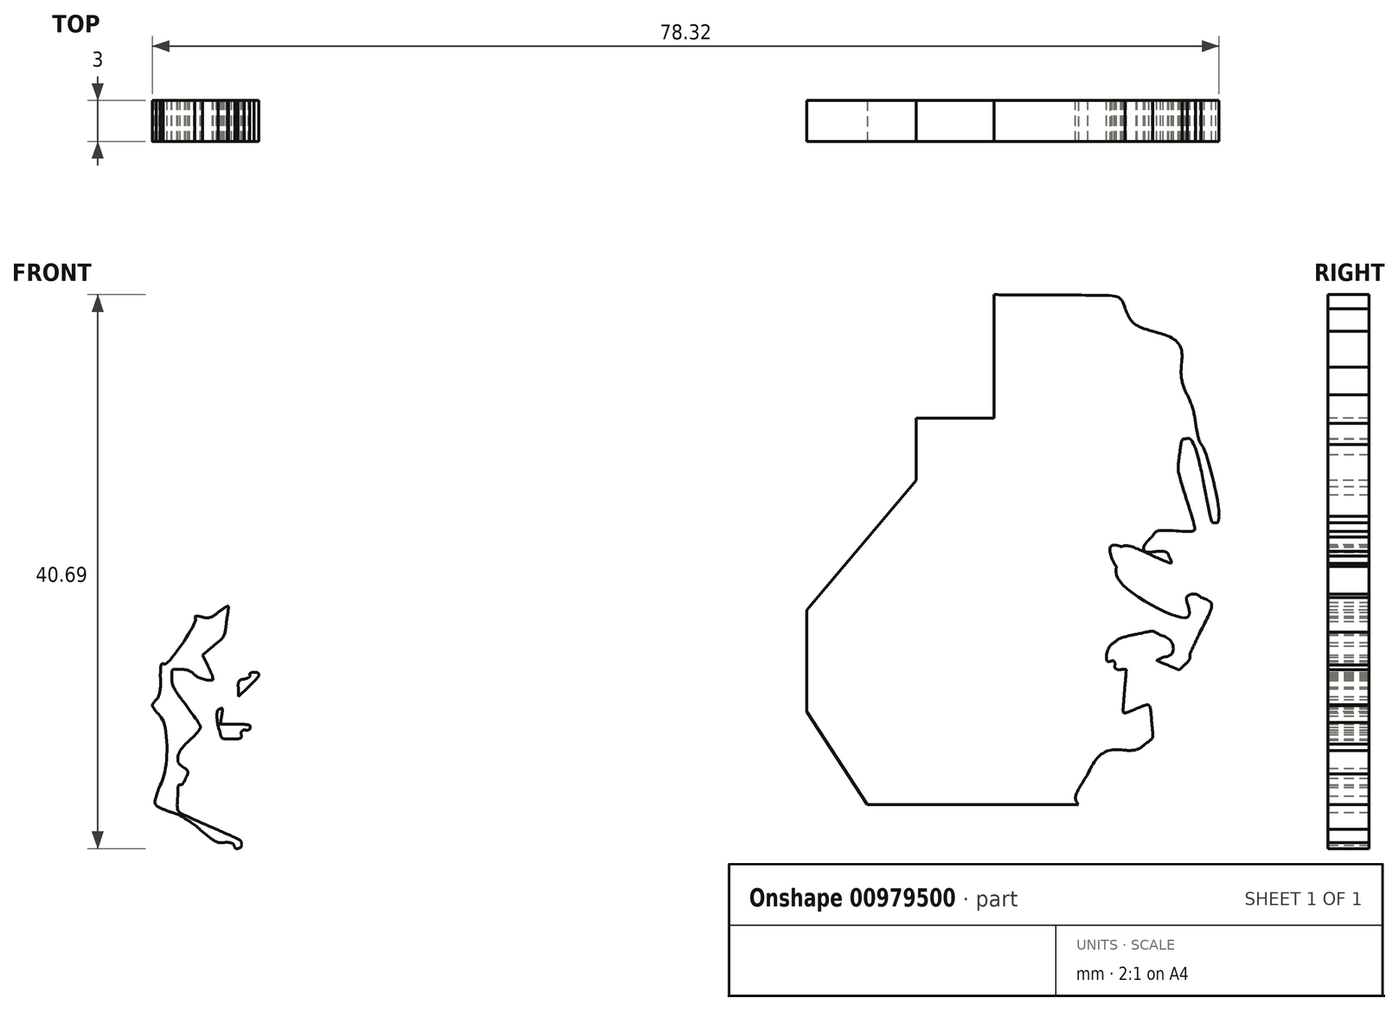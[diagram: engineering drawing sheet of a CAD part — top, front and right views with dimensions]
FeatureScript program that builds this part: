
annotation { "Feature Type Name" : "Feature", "Feature Type Description" : "" }
export const myFeature = defineFeature(function(context is Context, id is Id, definition is map)
    precondition{}
    {
        {
            var Q0;
            Q0=qCreatedBy(makeId("Front.planeOp"),FACE);
            var sketch = newSketch(context, id + "F0", { "sketchPlane" : qUnion([Q0])});
            skLineSegment(sketch, "E0", {"start": v(-32.88, 19.2) * mm, "end": v(-32.1, 20.83) * mm});
            skLineSegment(sketch, "E1", {"start": v(-32.1, 20.83) * mm, "end": v(-32.57, 22.16) * mm});
            skLineSegment(sketch, "E2", {"start": v(-27.5, 16.63) * mm, "end": v(-26.83, 16.28) * mm});
            skLineSegment(sketch, "E3", {"start": v(-26.83, 16.28) * mm, "end": v(-26.97, 16.83) * mm});
            skLineSegment(sketch, "E4", {"start": v(-24.85, 15.67) * mm, "end": v(-25.4, 15.88) * mm});
            skLineSegment(sketch, "E5", {"start": v(-25.4, 15.88) * mm, "end": v(-25.34, 18.4) * mm});
            skLineSegment(sketch, "E6", {"start": v(-1.75, 78.04) * mm, "end": v(-0.2, 79.6) * mm});
            skLineSegment(sketch, "E7", {"start": v(-0.2, 79.6) * mm, "end": v(1.27, 79.6) * mm});
            skLineSegment(sketch, "E8", {"start": v(38.3, 44.26) * mm, "end": v(38.3, 43.17) * mm});
            skLineSegment(sketch, "E9", {"start": v(38.3, 43.17) * mm, "end": v(37.62, 43.24) * mm});
            skLineSegment(sketch, "E10", {"start": v(39.65, -31.25) * mm, "end": v(39.52, -33.83) * mm});
            skLineSegment(sketch, "E11", {"start": v(39.52, -33.83) * mm, "end": v(40.18, -34.42) * mm});
            skLineSegment(sketch, "E12", {"start": v(1.4, 79.08) * mm, "end": v(0.3, 79.22) * mm});
            skLineSegment(sketch, "E13", {"start": v(0.3, 79.22) * mm, "end": v(-1.23, 77.67) * mm});
            skLineSegment(sketch, "E14", {"start": v(-12.51, 69.45) * mm, "end": v(-13.4, 69.45) * mm});
            skLineSegment(sketch, "E15", {"start": v(-13.4, 69.45) * mm, "end": v(-13.27, 67.07) * mm});
            skLineSegment(sketch, "E16", {"start": v(-18.31, 54.9) * mm, "end": v(-18.88, 53.48) * mm});
            skLineSegment(sketch, "E17", {"start": v(-18.88, 53.48) * mm, "end": v(-18.43, 53.1) * mm});
            skLineSegment(sketch, "E18", {"start": v(-20.94, 40.45) * mm, "end": v(-21.55, 40.45) * mm});
            skLineSegment(sketch, "E19", {"start": v(-21.55, 40.45) * mm, "end": v(-21.44, 41.8) * mm});
            skLineSegment(sketch, "E20", {"start": v(-24.47, 43.3) * mm, "end": v(-25.23, 42.61) * mm});
            skLineSegment(sketch, "E21", {"start": v(-25.23, 42.61) * mm, "end": v(-24.8, 41.05) * mm});
            skLineSegment(sketch, "E22", {"start": v(-37.96, -16.18) * mm, "end": v(-37.29, -17.23) * mm});
            skLineSegment(sketch, "E23", {"start": v(-37.29, -17.23) * mm, "end": v(-37.41, -20.41) * mm});
            skLineSegment(sketch, "E24", {"start": v(-30.4, -60.92) * mm, "end": v(-31.42, -62.04) * mm});
            skLineSegment(sketch, "E25", {"start": v(-31.42, -62.04) * mm, "end": v(-30.9, -63.02) * mm});
            skLineSegment(sketch, "E26", {"start": v(-36.35, 33.14) * mm, "end": v(-36.7, 33.88) * mm});
            skLineSegment(sketch, "E27", {"start": v(-36.7, 33.88) * mm, "end": v(-35.92, 34.57) * mm});
            skLineSegment(sketch, "E28", {"start": v(-34.09, 31.43) * mm, "end": v(-34.09, 30.84) * mm});
            skLineSegment(sketch, "E29", {"start": v(-34.09, 30.84) * mm, "end": v(-33.35, 31.56) * mm});
            skFitSpline(sketch, "E30", {"points": [v(-13.45, -80.7) * mm, v(-14.26, -80.4) * mm, v(-15.79, -79.86) * mm, v(-16.84, -79.51) * mm]});
            skFitSpline(sketch, "E31", {"points": [v(-16.84, -79.51) * mm, v(-20.43, -78.33) * mm, v(-20.6, -78.25) * mm, v(-21.55, -77.26) * mm]});
            skFitSpline(sketch, "E32", {"points": [v(-21.55, -77.26) * mm, v(-22.07, -76.72) * mm, v(-23.66, -74.52) * mm, v(-25.09, -72.37) * mm]});
            skFitSpline(sketch, "E33", {"points": [v(-25.09, -72.37) * mm, v(-26.52, -70.21) * mm, v(-28.36, -67.6) * mm, v(-29.19, -66.55) * mm]});
            skFitSpline(sketch, "E34", {"points": [v(-29.19, -66.55) * mm, v(-30.6, -64.76) * mm, v(-31.97, -62.53) * mm, v(-31.97, -62.03) * mm]});
            skFitSpline(sketch, "E35", {"points": [v(-31.97, -62.03) * mm, v(-31.97, -61.91) * mm, v(-31.5, -61.27) * mm, v(-30.92, -60.6) * mm]});
            skFitSpline(sketch, "E36", {"points": [v(-30.92, -60.6) * mm, v(-29.85, -59.39) * mm, v(-29, -57.92) * mm, v(-29, -57.28) * mm]});
            skFitSpline(sketch, "E37", {"points": [v(-29, -57.28) * mm, v(-29, -57.08) * mm, v(-29.34, -56.3) * mm, v(-29.75, -55.53) * mm]});
            skFitSpline(sketch, "E38", {"points": [v(-29.75, -55.53) * mm, v(-30.57, -53.98) * mm, v(-30.63, -53.57) * mm, v(-30.2, -52.72) * mm]});
            skFitSpline(sketch, "E39", {"points": [v(-30.2, -52.72) * mm, v(-29.95, -52.26) * mm, v(-29.92, -51.55) * mm, v(-30.04, -49.29) * mm]});
            skFitSpline(sketch, "E40", {"points": [v(-30.04, -49.29) * mm, v(-30.2, -46.13) * mm, v(-30.12, -46.32) * mm, v(-32.34, -43.6) * mm]});
            skFitSpline(sketch, "E41", {"points": [v(-32.34, -43.6) * mm, v(-32.83, -43) * mm, v(-33.38, -42.01) * mm, v(-33.55, -41.42) * mm]});
            skFitSpline(sketch, "E42", {"points": [v(-33.55, -41.42) * mm, v(-33.73, -40.84) * mm, v(-34.2, -39.94) * mm, v(-34.62, -39.44) * mm]});
            skFitSpline(sketch, "E43", {"points": [v(-34.62, -39.44) * mm, v(-36.03, -37.71) * mm, v(-36.52, -35.97) * mm, v(-35.98, -34.56) * mm]});
            skFitSpline(sketch, "E44", {"points": [v(-35.98, -34.56) * mm, v(-35.86, -34.24) * mm, v(-35.38, -33.57) * mm, v(-34.92, -33.07) * mm]});
            skFitSpline(sketch, "E45", {"points": [v(-34.92, -33.07) * mm, v(-33.97, -32.03) * mm, v(-34, -32.17) * mm, v(-34.37, -30.78) * mm]});
            skFitSpline(sketch, "E46", {"points": [v(-34.37, -30.78) * mm, v(-34.75, -29.38) * mm, v(-35.2, -28.53) * mm, v(-36.46, -26.88) * mm]});
            skFitSpline(sketch, "E47", {"points": [v(-36.46, -26.88) * mm, v(-37.04, -26.13) * mm, v(-37.61, -25.27) * mm, v(-37.73, -24.97) * mm]});
            skFitSpline(sketch, "E48", {"points": [v(-37.73, -24.97) * mm, v(-37.97, -24.39) * mm, v(-38.06, -21.07) * mm, v(-37.9, -18.8) * mm]});
            skFitSpline(sketch, "E49", {"points": [v(-37.9, -18.8) * mm, v(-37.82, -17.55) * mm, v(-37.87, -17.35) * mm, v(-38.39, -16.67) * mm]});
            skFitSpline(sketch, "E50", {"points": [v(-38.39, -16.67) * mm, v(-39.51, -15.19) * mm, v(-39.6, -12.77) * mm, v(-38.72, -7.81) * mm]});
            skFitSpline(sketch, "E51", {"points": [v(-38.72, -7.81) * mm, v(-38.24, -5.14) * mm, v(-38.31, -2.1) * mm, v(-38.87, -1) * mm]});
            skFitSpline(sketch, "E52", {"points": [v(-38.87, -1) * mm, v(-39.1, -0.56) * mm, v(-39.11, -0.29) * mm, v(-38.94, 0.17) * mm]});
            skFitSpline(sketch, "E53", {"points": [v(-38.94, 0.17) * mm, v(-38.62, 1) * mm, v(-38.87, 3.38) * mm, v(-39.5, 5.38) * mm]});
            skFitSpline(sketch, "E54", {"points": [v(-39.5, 5.38) * mm, v(-39.78, 6.29) * mm, v(-40.01, 7.26) * mm, v(-40.01, 7.54) * mm]});
            skFitSpline(sketch, "E55", {"points": [v(-40.01, 7.54) * mm, v(-40.01, 7.83) * mm, v(-39.68, 9.05) * mm, v(-39.27, 10.27) * mm]});
            skFitSpline(sketch, "E56", {"points": [v(-39.27, 10.27) * mm, v(-38.41, 12.85) * mm, v(-38.39, 13.06) * mm, v(-38.96, 13.2) * mm]});
            skFitSpline(sketch, "E57", {"points": [v(-38.96, 13.2) * mm, v(-39.71, 13.4) * mm, v(-39.48, 14.32) * mm, v(-38.38, 15.5) * mm]});
            skFitSpline(sketch, "E58", {"points": [v(-38.38, 15.5) * mm, v(-36.83, 17.16) * mm, v(-35.68, 17.57) * mm, v(-34.74, 16.8) * mm]});
            skFitSpline(sketch, "E59", {"points": [v(-34.74, 16.8) * mm, v(-34.08, 16.26) * mm, v(-32.77, 13.22) * mm, v(-32.66, 11.98) * mm]});
            skFitSpline(sketch, "E60", {"points": [v(-32.66, 11.98) * mm, v(-32.55, 10.86) * mm, v(-32.37, 10.61) * mm, v(-31.6, 10.6) * mm]});
            skFitSpline(sketch, "E61", {"points": [v(-31.6, 10.6) * mm, v(-31, 10.6) * mm, v(-30.96, 11.24) * mm, v(-31.55, 11.77) * mm]});
            skFitSpline(sketch, "E62", {"points": [v(-31.55, 11.77) * mm, v(-31.84, 12.03) * mm, v(-31.97, 12.42) * mm, v(-31.97, 13) * mm]});
            skFitSpline(sketch, "E63", {"points": [v(-31.97, 13) * mm, v(-31.97, 14.32) * mm, v(-32.62, 16.12) * mm, v(-33.18, 16.38) * mm]});
            skFitSpline(sketch, "E64", {"points": [v(-33.18, 16.38) * mm, v(-33.86, 16.69) * mm, v(-33.8, 17.27) * mm, v(-32.88, 19.2) * mm]});
            skFitSpline(sketch, "E65", {"points": [v(-32.57, 22.16) * mm, v(-32.82, 22.9) * mm, v(-33.03, 23.65) * mm, v(-33.03, 23.83) * mm]});
            skFitSpline(sketch, "E66", {"points": [v(-33.03, 23.83) * mm, v(-33.03, 24.1) * mm, v(-33.14, 24.14) * mm, v(-33.5, 24.01) * mm]});
            skFitSpline(sketch, "E67", {"points": [v(-33.5, 24.01) * mm, v(-33.77, 23.92) * mm, v(-34.4, 23.84) * mm, v(-34.93, 23.84) * mm]});
            skFitSpline(sketch, "E68", {"points": [v(-34.93, 23.84) * mm, v(-35.84, 23.83) * mm, v(-35.89, 23.86) * mm, v(-35.95, 24.48) * mm]});
            skFitSpline(sketch, "E69", {"points": [v(-35.95, 24.48) * mm, v(-36.05, 25.55) * mm, v(-34.78, 26.27) * mm, v(-32.78, 26.27) * mm]});
            skFitSpline(sketch, "E70", {"points": [v(-32.78, 26.27) * mm, v(-31.93, 26.27) * mm, v(-31.64, 26.16) * mm, v(-31.1, 25.65) * mm]});
            skFitSpline(sketch, "E71", {"points": [v(-31.1, 25.65) * mm, v(-30.75, 25.3) * mm, v(-30.32, 25.08) * mm, v(-30.15, 25.14) * mm]});
            skFitSpline(sketch, "E72", {"points": [v(-30.15, 25.14) * mm, v(-29.7, 25.31) * mm, v(-29.77, 25.47) * mm, v(-30.7, 26.37) * mm]});
            skFitSpline(sketch, "E73", {"points": [v(-30.7, 26.37) * mm, v(-31.5, 27.15) * mm, v(-31.55, 27.27) * mm, v(-31.55, 28.43) * mm]});
            skFitSpline(sketch, "E74", {"points": [v(-31.55, 28.43) * mm, v(-31.55, 29.6) * mm, v(-31.52, 29.65) * mm, v(-31.02, 29.65) * mm]});
            skFitSpline(sketch, "E75", {"points": [v(-31.02, 29.65) * mm, v(-30.7, 29.65) * mm, v(-30.49, 29.53) * mm, v(-30.49, 29.36) * mm]});
            skFitSpline(sketch, "E76", {"points": [v(-30.49, 29.36) * mm, v(-30.49, 28.94) * mm, v(-28.82, 27.75) * mm, v(-28.24, 27.75) * mm]});
            skFitSpline(sketch, "E77", {"points": [v(-28.24, 27.75) * mm, v(-27.83, 27.75) * mm, v(-27.75, 27.6) * mm, v(-27.62, 26.6) * mm]});
            skFitSpline(sketch, "E78", {"points": [v(-27.62, 26.6) * mm, v(-27.46, 25.26) * mm, v(-27.66, 24.55) * mm, v(-28.57, 23.22) * mm]});
            skFitSpline(sketch, "E79", {"points": [v(-28.57, 23.22) * mm, v(-29.21, 22.29) * mm, v(-29.4, 21.61) * mm, v(-29.02, 21.61) * mm]});
            skFitSpline(sketch, "E80", {"points": [v(-29.02, 21.61) * mm, v(-28.66, 21.61) * mm, v(-28.35, 20.18) * mm, v(-28.49, 19.14) * mm]});
            skFitSpline(sketch, "E81", {"points": [v(-28.49, 19.14) * mm, v(-28.66, 17.84) * mm, v(-28.36, 17.07) * mm, v(-27.5, 16.63) * mm]});
            skFitSpline(sketch, "E82", {"points": [v(-26.97, 16.83) * mm, v(-27.1, 17.33) * mm, v(-27.05, 17.38) * mm, v(-26.5, 17.38) * mm]});
            skFitSpline(sketch, "E83", {"points": [v(-26.5, 17.38) * mm, v(-25.81, 17.38) * mm, v(-25.62, 17.08) * mm, v(-25.62, 16.04) * mm]});
            skFitSpline(sketch, "E84", {"points": [v(-25.62, 16.04) * mm, v(-25.62, 15.5) * mm, v(-25.82, 15.19) * mm, v(-26.56, 14.52) * mm]});
            skFitSpline(sketch, "E85", {"points": [v(-26.56, 14.52) * mm, v(-27.09, 14.05) * mm, v(-27.58, 13.4) * mm, v(-27.66, 13.06) * mm]});
            skFitSpline(sketch, "E86", {"points": [v(-27.66, 13.06) * mm, v(-27.79, 12.49) * mm, v(-27.76, 12.45) * mm, v(-27.3, 12.58) * mm]});
            skFitSpline(sketch, "E87", {"points": [v(-27.3, 12.58) * mm, v(-27.01, 12.65) * mm, v(-26.47, 12.72) * mm, v(-26.09, 12.72) * mm]});
            skFitSpline(sketch, "E88", {"points": [v(-26.09, 12.72) * mm, v(-25.47, 12.72) * mm, v(-25.42, 12.76) * mm, v(-25.61, 13.13) * mm]});
            skFitSpline(sketch, "E89", {"points": [v(-25.61, 13.13) * mm, v(-26.02, 13.88) * mm, v(-25.88, 14.6) * mm, v(-25.31, 14.75) * mm]});
            skFitSpline(sketch, "E90", {"points": [v(-25.31, 14.75) * mm, v(-25.03, 14.82) * mm, v(-24.68, 15.01) * mm, v(-24.55, 15.17) * mm]});
            skFitSpline(sketch, "E91", {"points": [v(-24.55, 15.17) * mm, v(-24.35, 15.4) * mm, v(-24.42, 15.5) * mm, v(-24.85, 15.67) * mm]});
            skFitSpline(sketch, "E92", {"points": [v(-25.34, 18.4) * mm, v(-25.28, 20.49) * mm, v(-25.2, 21.05) * mm, v(-24.84, 21.66) * mm]});
            skFitSpline(sketch, "E93", {"points": [v(-24.84, 21.66) * mm, v(-24.6, 22.07) * mm, v(-24.33, 22.91) * mm, v(-24.25, 23.54) * mm]});
            skFitSpline(sketch, "E94", {"points": [v(-24.25, 23.54) * mm, v(-24.05, 24.98) * mm, v(-23.67, 25.42) * mm, v(-22.64, 25.42) * mm]});
            skFitSpline(sketch, "E95", {"points": [v(-22.64, 25.42) * mm, v(-21.97, 25.42) * mm, v(-21.73, 25.28) * mm, v(-21.09, 24.54) * mm]});
            skFitSpline(sketch, "E96", {"points": [v(-21.09, 24.54) * mm, v(-20.67, 24.05) * mm, v(-20.32, 23.55) * mm, v(-20.32, 23.43) * mm]});
            skFitSpline(sketch, "E97", {"points": [v(-20.32, 23.43) * mm, v(-20.3, 22.93) * mm, v(-19.5, 25.15) * mm, v(-19.5, 25.74) * mm]});
            skFitSpline(sketch, "E98", {"points": [v(-19.5, 25.74) * mm, v(-19.48, 26.68) * mm, v(-19.75, 27) * mm, v(-20.27, 26.68) * mm]});
            skFitSpline(sketch, "E99", {"points": [v(-20.27, 26.68) * mm, v(-20.84, 26.32) * mm, v(-23.7, 26.75) * mm, v(-24.99, 27.38) * mm]});
            skFitSpline(sketch, "E100", {"points": [v(-24.99, 27.38) * mm, v(-26.7, 28.23) * mm, v(-27.27, 29.95) * mm, v(-26.55, 32.07) * mm]});
            skFitSpline(sketch, "E101", {"points": [v(-26.55, 32.07) * mm, v(-26.23, 33) * mm, v(-26.23, 33.13) * mm, v(-26.58, 33.9) * mm]});
            skFitSpline(sketch, "E102", {"points": [v(-26.58, 33.9) * mm, v(-27.04, 34.91) * mm, v(-26.9, 36) * mm, v(-26.2, 36.92) * mm]});
            skFitSpline(sketch, "E103", {"points": [v(-26.2, 36.92) * mm, v(-24.96, 38.54) * mm, v(-24.76, 39.42) * mm, v(-25.3, 40.73) * mm]});
            skFitSpline(sketch, "E104", {"points": [v(-25.3, 40.73) * mm, v(-25.48, 41.15) * mm, v(-25.62, 41.87) * mm, v(-25.62, 42.33) * mm]});
            skFitSpline(sketch, "E105", {"points": [v(-25.62, 42.33) * mm, v(-25.62, 43.02) * mm, v(-25.5, 43.25) * mm, v(-24.99, 43.62) * mm]});
            skFitSpline(sketch, "E106", {"points": [v(-24.99, 43.62) * mm, v(-24.64, 43.87) * mm, v(-24.35, 44.26) * mm, v(-24.35, 44.48) * mm]});
            skFitSpline(sketch, "E107", {"points": [v(-24.35, 44.48) * mm, v(-24.35, 45.6) * mm, v(-22.43, 46.16) * mm, v(-21.62, 45.29) * mm]});
            skFitSpline(sketch, "E108", {"points": [v(-21.62, 45.29) * mm, v(-21.1, 44.74) * mm, v(-20.66, 42.78) * mm, v(-20.82, 41.8) * mm]});
            skFitSpline(sketch, "E109", {"points": [v(-20.82, 41.8) * mm, v(-20.95, 40.98) * mm, v(-20.5, 40.8) * mm, v(-20.12, 41.5) * mm]});
            skFitSpline(sketch, "E110", {"points": [v(-20.12, 41.5) * mm, v(-20, 41.74) * mm, v(-19.7, 41.93) * mm, v(-19.48, 41.93) * mm]});
            skFitSpline(sketch, "E111", {"points": [v(-19.48, 41.93) * mm, v(-19.2, 41.93) * mm, v(-19.03, 42.12) * mm, v(-18.95, 42.51) * mm]});
            skFitSpline(sketch, "E112", {"points": [v(-18.95, 42.51) * mm, v(-18.9, 42.83) * mm, v(-18.75, 43.5) * mm, v(-18.63, 44) * mm]});
            skFitSpline(sketch, "E113", {"points": [v(-18.63, 44) * mm, v(-18.15, 46.1) * mm, v(-18.46, 46.83) * mm, v(-19.95, 47.1) * mm]});
            skFitSpline(sketch, "E114", {"points": [v(-19.95, 47.1) * mm, v(-21.37, 47.35) * mm, v(-21.68, 48.31) * mm, v(-21.02, 50.45) * mm]});
            skFitSpline(sketch, "E115", {"points": [v(-21.02, 50.45) * mm, v(-20.67, 51.58) * mm, v(-20.6, 51.66) * mm, v(-20, 51.67) * mm]});
            skFitSpline(sketch, "E116", {"points": [v(-20, 51.67) * mm, v(-19.64, 51.67) * mm, v(-19.17, 51.8) * mm, v(-18.94, 51.97) * mm]});
            skFitSpline(sketch, "E117", {"points": [v(-18.94, 51.97) * mm, v(-18.56, 52.25) * mm, v(-18.55, 52.28) * mm, v(-18.9, 52.67) * mm]});
            skFitSpline(sketch, "E118", {"points": [v(-18.9, 52.67) * mm, v(-19.36, 53.18) * mm, v(-19.37, 53.99) * mm, v(-18.93, 55) * mm]});
            skFitSpline(sketch, "E119", {"points": [v(-18.93, 55) * mm, v(-18.26, 56.57) * mm, v(-18.22, 56.96) * mm, v(-18.55, 58.71) * mm]});
            skFitSpline(sketch, "E120", {"points": [v(-18.55, 58.71) * mm, v(-19.05, 61.35) * mm, v(-18.66, 63.1) * mm, v(-17.57, 63.1) * mm]});
            skFitSpline(sketch, "E121", {"points": [v(-17.57, 63.1) * mm, v(-17.13, 63.1) * mm, v(-16.93, 62.86) * mm, v(-16.62, 61.94) * mm]});
            skFitSpline(sketch, "E122", {"points": [v(-16.62, 61.94) * mm, v(-16.19, 60.62) * mm, v(-15.25, 61.36) * mm, v(-15.25, 63.03) * mm]});
            skFitSpline(sketch, "E123", {"points": [v(-15.25, 63.03) * mm, v(-15.25, 63.72) * mm, v(-15.21, 63.77) * mm, v(-14.72, 63.65) * mm]});
            skFitSpline(sketch, "E124", {"points": [v(-14.72, 63.65) * mm, v(-13.88, 63.44) * mm, v(-13.7, 64.21) * mm, v(-13.86, 67.25) * mm]});
            skFitSpline(sketch, "E125", {"points": [v(-13.86, 67.25) * mm, v(-14.01, 70.15) * mm, v(-14.06, 70.07) * mm, v(-12.21, 70.08) * mm]});
            skFitSpline(sketch, "E126", {"points": [v(-12.21, 70.08) * mm, v(-11.52, 70.08) * mm, v(-11.25, 70.23) * mm, v(-10.4, 71.12) * mm]});
            skFitSpline(sketch, "E127", {"points": [v(-10.4, 71.12) * mm, v(-9.38, 72.18) * mm, v(-9.03, 72.34) * mm, v(-6.52, 72.84) * mm]});
            skFitSpline(sketch, "E128", {"points": [v(-6.52, 72.84) * mm, v(-4.93, 73.15) * mm, v(-4.21, 73.78) * mm, v(-3.7, 75.27) * mm]});
            skFitSpline(sketch, "E129", {"points": [v(-3.7, 75.27) * mm, v(-3.38, 76.2) * mm, v(-2.96, 76.8) * mm, v(-1.75, 78.04) * mm]});
            skFitSpline(sketch, "E130", {"points": [v(1.27, 79.6) * mm, v(2.66, 79.6) * mm, v(2.79, 79.65) * mm, v(3.57, 80.36) * mm]});
            skFitSpline(sketch, "E131", {"points": [v(3.57, 80.36) * mm, v(4.72, 81.4) * mm, v(5.62, 81.51) * mm, v(6.84, 80.8) * mm]});
            skFitSpline(sketch, "E132", {"points": [v(6.84, 80.8) * mm, v(7.4, 80.48) * mm, v(8.11, 80.24) * mm, v(8.56, 80.24) * mm]});
            skFitSpline(sketch, "E133", {"points": [v(8.56, 80.24) * mm, v(9.65, 80.24) * mm, v(10.66, 79.76) * mm, v(12.03, 78.58) * mm]});
            skFitSpline(sketch, "E134", {"points": [v(12.03, 78.58) * mm, v(12.68, 78.02) * mm, v(13.76, 77.21) * mm, v(14.43, 76.8) * mm]});
            skFitSpline(sketch, "E135", {"points": [v(14.43, 76.8) * mm, v(16.07, 75.75) * mm, v(16.3, 75.23) * mm, v(16.26, 72.68) * mm]});
            skFitSpline(sketch, "E136", {"points": [v(16.26, 72.68) * mm, v(16.21, 70.3) * mm, v(16.3, 70.06) * mm, v(17.99, 67.97) * mm]});
            skFitSpline(sketch, "E137", {"points": [v(17.99, 67.97) * mm, v(19.34, 66.28) * mm, v(19.58, 65.73) * mm, v(19.78, 63.84) * mm]});
            skFitSpline(sketch, "E138", {"points": [v(19.78, 63.84) * mm, v(19.97, 61.97) * mm, v(20.1, 61.75) * mm, v(21.2, 61.28) * mm]});
            skFitSpline(sketch, "E139", {"points": [v(21.2, 61.28) * mm, v(21.95, 60.97) * mm, v(22.77, 60.9) * mm, v(25.95, 60.87) * mm]});
            skFitSpline(sketch, "E140", {"points": [v(25.95, 60.87) * mm, v(29.47, 60.83) * mm, v(29.87, 60.8) * mm, v(30.78, 60.35) * mm]});
            skFitSpline(sketch, "E141", {"points": [v(30.78, 60.35) * mm, v(31.33, 60.09) * mm, v(31.82, 59.71) * mm, v(31.88, 59.53) * mm]});
            skFitSpline(sketch, "E142", {"points": [v(31.88, 59.53) * mm, v(32.1, 58.78) * mm, v(32.32, 58.58) * mm, v(33.34, 58.19) * mm]});
            skFitSpline(sketch, "E143", {"points": [v(33.34, 58.19) * mm, v(35, 57.54) * mm, v(35.47, 56.96) * mm, v(35.61, 55.41) * mm]});
            skFitSpline(sketch, "E144", {"points": [v(35.61, 55.41) * mm, v(35.68, 54.7) * mm, v(35.93, 53.67) * mm, v(36.17, 53.15) * mm]});
            skFitSpline(sketch, "E145", {"points": [v(36.17, 53.15) * mm, v(36.4, 52.63) * mm, v(36.6, 51.94) * mm, v(36.6, 51.62) * mm]});
            skFitSpline(sketch, "E146", {"points": [v(36.6, 51.62) * mm, v(36.6, 51.3) * mm, v(36.8, 50.55) * mm, v(37.02, 49.93) * mm]});
            skFitSpline(sketch, "E147", {"points": [v(37.02, 49.93) * mm, v(37.7, 48.08) * mm, v(38.3, 45.42) * mm, v(38.3, 44.26) * mm]});
            skFitSpline(sketch, "E148", {"points": [v(37.62, 43.24) * mm, v(36.87, 43.31) * mm, v(36.86, 43.33) * mm, v(36.05, 46.9) * mm]});
            skFitSpline(sketch, "E149", {"points": [v(36.05, 46.9) * mm, v(35.75, 48.23) * mm, v(35.65, 48.45) * mm, v(35.6, 47.92) * mm]});
            skFitSpline(sketch, "E150", {"points": [v(35.6, 47.92) * mm, v(35.56, 47.55) * mm, v(35.72, 46.61) * mm, v(35.96, 45.84) * mm]});
            skFitSpline(sketch, "E151", {"points": [v(35.96, 45.84) * mm, v(36.2, 45.06) * mm, v(36.4, 44.16) * mm, v(36.4, 43.83) * mm]});
            skFitSpline(sketch, "E152", {"points": [v(36.4, 43.83) * mm, v(36.4, 42.72) * mm, v(36.23, 42.57) * mm, v(35.04, 42.57) * mm]});
            skFitSpline(sketch, "E153", {"points": [v(35.04, 42.57) * mm, v(34.35, 42.57) * mm, v(33.78, 42.44) * mm, v(33.53, 42.23) * mm]});
            skFitSpline(sketch, "E154", {"points": [v(33.53, 42.23) * mm, v(33.14, 41.92) * mm, v(33.15, 41.9) * mm, v(33.78, 42.01) * mm]});
            skFitSpline(sketch, "E155", {"points": [v(33.78, 42.01) * mm, v(34.37, 42.1) * mm, v(34.48, 42.05) * mm, v(34.7, 41.5) * mm]});
            skFitSpline(sketch, "E156", {"points": [v(34.7, 41.5) * mm, v(35.23, 40.23) * mm, v(34.46, 39.89) * mm, v(32.77, 40.66) * mm]});
            skFitSpline(sketch, "E157", {"points": [v(32.77, 40.66) * mm, v(30, 41.91) * mm, v(30.46, 40.26) * mm, v(33.3, 38.77) * mm]});
            skFitSpline(sketch, "E158", {"points": [v(33.3, 38.77) * mm, v(34.7, 38.04) * mm, v(35.03, 37.98) * mm, v(35.2, 38.44) * mm]});
            skFitSpline(sketch, "E159", {"points": [v(35.2, 38.44) * mm, v(35.4, 38.97) * mm, v(36.94, 38.86) * mm, v(37.34, 38.29) * mm]});
            skFitSpline(sketch, "E160", {"points": [v(37.34, 38.29) * mm, v(37.8, 37.64) * mm, v(37.75, 36.5) * mm, v(37.25, 35.69) * mm]});
            skFitSpline(sketch, "E161", {"points": [v(37.25, 35.69) * mm, v(37.01, 35.31) * mm, v(36.68, 34.6) * mm, v(36.5, 34.09) * mm]});
            skFitSpline(sketch, "E162", {"points": [v(36.5, 34.09) * mm, v(36.07, 32.87) * mm, v(35.62, 32.4) * mm, v(34.86, 32.4) * mm]});
            skFitSpline(sketch, "E163", {"points": [v(34.86, 32.4) * mm, v(34.06, 32.4) * mm, v(32.85, 32.98) * mm, v(32.57, 33.5) * mm]});
            skFitSpline(sketch, "E164", {"points": [v(32.57, 33.5) * mm, v(32.35, 33.9) * mm, v(32.37, 33.91) * mm, v(33.4, 34.23) * mm]});
            skFitSpline(sketch, "E165", {"points": [v(33.4, 34.23) * mm, v(33.55, 34.27) * mm, v(33.64, 34.43) * mm, v(33.6, 34.58) * mm]});
            skFitSpline(sketch, "E166", {"points": [v(33.6, 34.58) * mm, v(33.47, 34.97) * mm, v(32.1, 35.02) * mm, v(31.26, 34.66) * mm]});
            skFitSpline(sketch, "E167", {"points": [v(31.26, 34.66) * mm, v(30.63, 34.4) * mm, v(30.54, 34.27) * mm, v(30.63, 33.8) * mm]});
            skFitSpline(sketch, "E168", {"points": [v(30.63, 33.8) * mm, v(30.71, 33.37) * mm, v(30.83, 33.27) * mm, v(31.13, 33.37) * mm]});
            skFitSpline(sketch, "E169", {"points": [v(31.13, 33.37) * mm, v(31.68, 33.54) * mm, v(31.8, 33.13) * mm, v(31.57, 31.7) * mm]});
            skFitSpline(sketch, "E170", {"points": [v(31.57, 31.7) * mm, v(31.47, 31.04) * mm, v(31.4, 30.5) * mm, v(31.43, 30.5) * mm]});
            skFitSpline(sketch, "E171", {"points": [v(31.43, 30.5) * mm, v(31.46, 30.5) * mm, v(31.82, 30.65) * mm, v(32.25, 30.82) * mm]});
            skFitSpline(sketch, "E172", {"points": [v(32.25, 30.82) * mm, v(33.01, 31.14) * mm, v(33.02, 31.14) * mm, v(33.26, 30.56) * mm]});
            skFitSpline(sketch, "E173", {"points": [v(33.26, 30.56) * mm, v(33.39, 30.24) * mm, v(33.5, 29.43) * mm, v(33.52, 28.77) * mm]});
            skFitSpline(sketch, "E174", {"points": [v(33.52, 28.77) * mm, v(33.55, 27.14) * mm, v(33.03, 26.57) * mm, v(31.4, 26.43) * mm]});
            skFitSpline(sketch, "E175", {"points": [v(31.4, 26.43) * mm, v(29.99, 26.32) * mm, v(29.27, 25.83) * mm, v(28.59, 24.5) * mm]});
            skFitSpline(sketch, "E176", {"points": [v(28.59, 24.5) * mm, v(28.09, 23.52) * mm, v(28.09, 23.5) * mm, v(28.46, 22.8) * mm]});
            skFitSpline(sketch, "E177", {"points": [v(28.46, 22.8) * mm, v(29.02, 21.76) * mm, v(28.8, 20.5) * mm, v(27.76, 18.77) * mm]});
            skFitSpline(sketch, "E178", {"points": [v(27.76, 18.77) * mm, v(26.26, 16.28) * mm, v(26.34, 15.6) * mm, v(28.5, 12.89) * mm]});
            skFitSpline(sketch, "E179", {"points": [v(28.5, 12.89) * mm, v(30.07, 10.9) * mm, v(30.64, 9.85) * mm, v(31.32, 7.7) * mm]});
            skFitSpline(sketch, "E180", {"points": [v(31.32, 7.7) * mm, v(31.79, 6.2) * mm, v(31.8, 6.14) * mm, v(31.41, 5.73) * mm]});
            skFitSpline(sketch, "E181", {"points": [v(31.41, 5.73) * mm, v(31.08, 5.36) * mm, v(31.06, 5.2) * mm, v(31.28, 4.6) * mm]});
            skFitSpline(sketch, "E182", {"points": [v(31.28, 4.6) * mm, v(31.65, 3.58) * mm, v(31.59, 2.92) * mm, v(31, 1.59) * mm]});
            skFitSpline(sketch, "E183", {"points": [v(31, 1.59) * mm, v(30.4, 0.22) * mm, v(30.37, 0) * mm, v(30.73, -0.98) * mm]});
            skFitSpline(sketch, "E184", {"points": [v(30.73, -0.98) * mm, v(30.96, -1.6) * mm, v(30.93, -1.79) * mm, v(30.48, -2.62) * mm]});
            skFitSpline(sketch, "E185", {"points": [v(30.48, -2.62) * mm, v(29.76, -3.92) * mm, v(30.03, -4.4) * mm, v(31.97, -5.39) * mm]});
            skFitSpline(sketch, "E186", {"points": [v(31.97, -5.39) * mm, v(33.32, -6.07) * mm, v(33.55, -6.12) * mm, v(34.1, -5.9) * mm]});
            skFitSpline(sketch, "E187", {"points": [v(34.1, -5.9) * mm, v(34.89, -5.57) * mm, v(35.48, -5.74) * mm, v(36.67, -6.64) * mm]});
            skFitSpline(sketch, "E188", {"points": [v(36.67, -6.64) * mm, v(37.21, -7.06) * mm, v(37.94, -7.45) * mm, v(38.28, -7.52) * mm]});
            skFitSpline(sketch, "E189", {"points": [v(38.28, -7.52) * mm, v(38.74, -7.61) * mm, v(38.97, -7.82) * mm, v(39.14, -8.29) * mm]});
            skFitSpline(sketch, "E190", {"points": [v(39.14, -8.29) * mm, v(39.46, -9.22) * mm, v(39.43, -9.36) * mm, v(38.73, -10.24) * mm]});
            skFitSpline(sketch, "E191", {"points": [v(38.73, -10.24) * mm, v(37.95, -11.22) * mm, v(37.9, -12.13) * mm, v(38.57, -13.12) * mm]});
            skFitSpline(sketch, "E192", {"points": [v(38.57, -13.12) * mm, v(38.94, -13.67) * mm, v(39.23, -13.86) * mm, v(39.79, -13.91) * mm]});
            skFitSpline(sketch, "E193", {"points": [v(39.79, -13.91) * mm, v(40.2, -13.95) * mm, v(40.6, -14.1) * mm, v(40.68, -14.23) * mm]});
            skFitSpline(sketch, "E194", {"points": [v(40.68, -14.23) * mm, v(40.98, -14.7) * mm, v(40.84, -15.58) * mm, v(40.4, -15.98) * mm]});
            skFitSpline(sketch, "E195", {"points": [v(40.4, -15.98) * mm, v(40.04, -16.3) * mm, v(39.97, -16.56) * mm, v(40.05, -17.26) * mm]});
            skFitSpline(sketch, "E196", {"points": [v(40.05, -17.26) * mm, v(40.14, -18.03) * mm, v(40.09, -18.17) * mm, v(39.65, -18.37) * mm]});
            skFitSpline(sketch, "E197", {"points": [v(39.65, -18.37) * mm, v(39.06, -18.64) * mm, v(39.03, -18.9) * mm, v(39.5, -20) * mm]});
            skFitSpline(sketch, "E198", {"points": [v(39.5, -20) * mm, v(39.77, -20.67) * mm, v(39.83, -21.57) * mm, v(39.81, -24.74) * mm]});
            skFitSpline(sketch, "E199", {"points": [v(39.81, -24.74) * mm, v(39.8, -26.9) * mm, v(39.73, -29.82) * mm, v(39.65, -31.25) * mm]});
            skFitSpline(sketch, "E200", {"points": [v(40.18, -34.42) * mm, v(40.54, -34.74) * mm, v(40.84, -35.18) * mm, v(40.84, -35.41) * mm]});
            skFitSpline(sketch, "E201", {"points": [v(40.84, -35.41) * mm, v(40.84, -36.27) * mm, v(39.96, -37.65) * mm, v(38.92, -38.41) * mm]});
            skFitSpline(sketch, "E202", {"points": [v(38.92, -38.41) * mm, v(37.63, -39.36) * mm, v(37.28, -40) * mm, v(37.05, -41.89) * mm]});
            skFitSpline(sketch, "E203", {"points": [v(37.05, -41.89) * mm, v(36.94, -42.7) * mm, v(36.66, -43.77) * mm, v(36.42, -44.27) * mm]});
            skFitSpline(sketch, "E204", {"points": [v(36.42, -44.27) * mm, v(35.96, -45.22) * mm, v(33.78, -47.87) * mm, v(31.3, -50.5) * mm]});
            skFitSpline(sketch, "E205", {"points": [v(31.3, -50.5) * mm, v(29.02, -52.92) * mm, v(27.8, -55.66) * mm, v(27.2, -59.77) * mm]});
            skFitSpline(sketch, "E206", {"points": [v(27.2, -59.77) * mm, v(26.85, -62.13) * mm, v(26.75, -62.37) * mm, v(25.14, -65) * mm]});
            skFitSpline(sketch, "E207", {"points": [v(25.14, -65) * mm, v(24.58, -65.91) * mm, v(24.35, -66.6) * mm, v(24.16, -67.9) * mm]});
            skFitSpline(sketch, "E208", {"points": [v(24.16, -67.9) * mm, v(23.88, -69.93) * mm, v(23.36, -71.03) * mm, v(22.29, -71.92) * mm]});
            skFitSpline(sketch, "E209", {"points": [v(22.29, -71.92) * mm, v(21.43, -72.63) * mm, v(19.94, -73.22) * mm, v(19, -73.22) * mm]});
            skFitSpline(sketch, "E210", {"points": [v(19, -73.22) * mm, v(18.6, -73.22) * mm, v(18.4, -73.32) * mm, v(18.4, -73.56) * mm]});
            skFitSpline(sketch, "E211", {"points": [v(18.4, -73.56) * mm, v(18.4, -73.75) * mm, v(18.21, -74.22) * mm, v(17.97, -74.6) * mm]});
            skFitSpline(sketch, "E212", {"points": [v(17.97, -74.6) * mm, v(17.57, -75.26) * mm, v(17.56, -75.35) * mm, v(17.87, -76.08) * mm]});
            skFitSpline(sketch, "E213", {"points": [v(17.87, -76.08) * mm, v(18.34, -77.22) * mm, v(18.3, -77.38) * mm, v(17.14, -78.58) * mm]});
            skFitSpline(sketch, "E214", {"points": [v(17.14, -78.58) * mm, v(16.56, -79.18) * mm, v(15.87, -79.93) * mm, v(15.6, -80.25) * mm]});
            skFitSpline(sketch, "E215", {"points": [v(15.6, -80.25) * mm, v(15.34, -80.56) * mm, v(14.86, -80.88) * mm, v(14.54, -80.96) * mm]});
            skFitSpline(sketch, "E216", {"points": [v(14.54, -80.96) * mm, v(14.03, -81.08) * mm, v(13.96, -81.03) * mm, v(13.96, -80.56) * mm]});
            skFitSpline(sketch, "E217", {"points": [v(13.96, -80.56) * mm, v(13.96, -80.25) * mm, v(13.75, -79.86) * mm, v(13.47, -79.63) * mm]});
            skFitSpline(sketch, "E218", {"points": [v(13.47, -79.63) * mm, v(12.33, -78.73) * mm, v(12.3, -77.45) * mm, v(13.44, -77.45) * mm]});
            skFitSpline(sketch, "E219", {"points": [v(13.44, -77.45) * mm, v(14.2, -77.45) * mm, v(15.11, -76) * mm, v(14.94, -75.07) * mm]});
            skFitSpline(sketch, "E220", {"points": [v(14.94, -75.07) * mm, v(14.87, -74.7) * mm, v(14.75, -74.02) * mm, v(14.67, -73.57) * mm]});
            skFitSpline(sketch, "E221", {"points": [v(14.67, -73.57) * mm, v(14.58, -73.02) * mm, v(14.45, -72.8) * mm, v(14.25, -72.88) * mm]});
            skFitSpline(sketch, "E222", {"points": [v(14.25, -72.88) * mm, v(14.1, -72.94) * mm, v(13.13, -72.88) * mm, v(12.11, -72.76) * mm]});
            skFitSpline(sketch, "E223", {"points": [v(12.11, -72.76) * mm, v(10.8, -72.6) * mm, v(10.12, -72.4) * mm, v(9.8, -72.1) * mm]});
            skFitSpline(sketch, "E224", {"points": [v(9.8, -72.1) * mm, v(9.32, -71.67) * mm, v(8.88, -71.75) * mm, v(8.88, -72.28) * mm]});
            skFitSpline(sketch, "E225", {"points": [v(8.88, -72.28) * mm, v(8.88, -72.66) * mm, v(8.5, -72.65) * mm, v(7.82, -72.26) * mm]});
            skFitSpline(sketch, "E226", {"points": [v(7.82, -72.26) * mm, v(7.11, -71.86) * mm, v(5.83, -71.87) * mm, v(4.94, -72.29) * mm]});
            skFitSpline(sketch, "E227", {"points": [v(4.94, -72.29) * mm, v(4.16, -72.66) * mm, v(4.18, -72.61) * mm, v(4.14, -74.27) * mm]});
            skFitSpline(sketch, "E228", {"points": [v(4.14, -74.27) * mm, v(4.12, -75.43) * mm, v(4.11, -75.44) * mm, v(3.17, -75.91) * mm]});
            skFitSpline(sketch, "E229", {"points": [v(3.17, -75.91) * mm, v(2.65, -76.18) * mm, v(1.84, -76.77) * mm, v(1.36, -77.24) * mm]});
            skFitSpline(sketch, "E230", {"points": [v(1.36, -77.24) * mm, v(0.68, -77.91) * mm, v(-0.19, -78.37) * mm, v(-2.67, -79.37) * mm]});
            skFitSpline(sketch, "E231", {"points": [v(-2.67, -79.37) * mm, v(-6.5, -80.92) * mm, v(-7.82, -81.25) * mm, v(-10.17, -81.25) * mm]});
            skFitSpline(sketch, "E232", {"points": [v(-10.17, -81.25) * mm, v(-11.59, -81.25) * mm, v(-12.28, -81.13) * mm, v(-13.45, -80.7) * mm]});
            skFitSpline(sketch, "E233", {"points": [v(-6.84, -80.3) * mm, v(-6.29, -80.14) * mm, v(-4.56, -79.5) * mm, v(-3, -78.88) * mm]});
            skFitSpline(sketch, "E234", {"points": [v(-3, -78.88) * mm, v(-0.66, -77.96) * mm, v(0.05, -77.57) * mm, v(1.08, -76.65) * mm]});
            skFitSpline(sketch, "E235", {"points": [v(1.08, -76.65) * mm, v(1.77, -76.04) * mm, v(2.46, -75.54) * mm, v(2.62, -75.54) * mm]});
            skFitSpline(sketch, "E236", {"points": [v(2.62, -75.54) * mm, v(2.78, -75.54) * mm, v(3.12, -75.37) * mm, v(3.38, -75.16) * mm]});
            skFitSpline(sketch, "E237", {"points": [v(3.38, -75.16) * mm, v(3.8, -74.81) * mm, v(3.83, -74.72) * mm, v(3.59, -73.93) * mm]});
            skFitSpline(sketch, "E238", {"points": [v(3.59, -73.93) * mm, v(3.4, -73.28) * mm, v(3.39, -72.96) * mm, v(3.57, -72.61) * mm]});
            skFitSpline(sketch, "E239", {"points": [v(3.57, -72.61) * mm, v(4.07, -71.69) * mm, v(6.12, -71.11) * mm, v(7.53, -71.5) * mm]});
            skFitSpline(sketch, "E240", {"points": [v(7.53, -71.5) * mm, v(8.17, -71.68) * mm, v(8.4, -71.66) * mm, v(8.68, -71.41) * mm]});
            skFitSpline(sketch, "E241", {"points": [v(8.68, -71.41) * mm, v(9.15, -70.98) * mm, v(9.64, -71.02) * mm, v(10.13, -71.54) * mm]});
            skFitSpline(sketch, "E242", {"points": [v(10.13, -71.54) * mm, v(10.44, -71.88) * mm, v(10.95, -72.03) * mm, v(12.2, -72.17) * mm]});
            skFitSpline(sketch, "E243", {"points": [v(12.2, -72.17) * mm, v(13.1, -72.28) * mm, v(14, -72.32) * mm, v(14.17, -72.26) * mm]});
            skFitSpline(sketch, "E244", {"points": [v(14.17, -72.26) * mm, v(14.75, -72.09) * mm, v(15.04, -72.5) * mm, v(15.33, -73.91) * mm]});
            skFitSpline(sketch, "E245", {"points": [v(15.33, -73.91) * mm, v(15.54, -74.89) * mm, v(15.57, -75.53) * mm, v(15.43, -76.04) * mm]});
            skFitSpline(sketch, "E246", {"points": [v(15.43, -76.04) * mm, v(15.14, -77.06) * mm, v(14.45, -77.87) * mm, v(13.85, -77.87) * mm]});
            skFitSpline(sketch, "E247", {"points": [v(13.85, -77.87) * mm, v(13.06, -77.87) * mm, v(13.01, -78.27) * mm, v(13.7, -79) * mm]});
            skFitSpline(sketch, "E248", {"points": [v(13.7, -79) * mm, v(14.06, -79.37) * mm, v(14.38, -79.86) * mm, v(14.43, -80.1) * mm]});
            skFitSpline(sketch, "E249", {"points": [v(14.43, -80.1) * mm, v(14.5, -80.48) * mm, v(14.55, -80.47) * mm, v(15.03, -79.9) * mm]});
            skFitSpline(sketch, "E250", {"points": [v(15.03, -79.9) * mm, v(15.31, -79.57) * mm, v(16.02, -78.83) * mm, v(16.6, -78.28) * mm]});
            skFitSpline(sketch, "E251", {"points": [v(16.6, -78.28) * mm, v(17.64, -77.28) * mm, v(17.65, -77.26) * mm, v(17.4, -76.55) * mm]});
            skFitSpline(sketch, "E252", {"points": [v(17.4, -76.55) * mm, v(17.05, -75.6) * mm, v(17.07, -74.87) * mm, v(17.45, -74.37) * mm]});
            skFitSpline(sketch, "E253", {"points": [v(17.45, -74.37) * mm, v(17.62, -74.14) * mm, v(17.76, -73.7) * mm, v(17.76, -73.4) * mm]});
            skFitSpline(sketch, "E254", {"points": [v(17.76, -73.4) * mm, v(17.77, -72.89) * mm, v(17.86, -72.83) * mm, v(18.88, -72.7) * mm]});
            skFitSpline(sketch, "E255", {"points": [v(18.88, -72.7) * mm, v(19.5, -72.62) * mm, v(20.47, -72.3) * mm, v(21.04, -71.99) * mm]});
            skFitSpline(sketch, "E256", {"points": [v(21.04, -71.99) * mm, v(22.45, -71.22) * mm, v(23.22, -70.08) * mm, v(23.5, -68.35) * mm]});
            skFitSpline(sketch, "E257", {"points": [v(23.5, -68.35) * mm, v(23.9, -65.9) * mm, v(24.16, -65.2) * mm, v(25.1, -63.87) * mm]});
            skFitSpline(sketch, "E258", {"points": [v(25.1, -63.87) * mm, v(26.18, -62.33) * mm, v(26.35, -61.85) * mm, v(26.67, -59.46) * mm]});
            skFitSpline(sketch, "E259", {"points": [v(26.67, -59.46) * mm, v(26.98, -57.13) * mm, v(27.93, -54.18) * mm, v(28.89, -52.58) * mm]});
            skFitSpline(sketch, "E260", {"points": [v(28.89, -52.58) * mm, v(29.3, -51.88) * mm, v(30.25, -50.69) * mm, v(31, -49.93) * mm]});
            skFitSpline(sketch, "E261", {"points": [v(31, -49.93) * mm, v(33.26, -47.61) * mm, v(35.36, -45.01) * mm, v(35.9, -43.88) * mm]});
            skFitSpline(sketch, "E262", {"points": [v(35.9, -43.88) * mm, v(36.17, -43.28) * mm, v(36.49, -42.11) * mm, v(36.6, -41.27) * mm]});
            skFitSpline(sketch, "E263", {"points": [v(36.6, -41.27) * mm, v(36.81, -39.5) * mm, v(37.06, -39.06) * mm, v(38.37, -38.07) * mm]});
            skFitSpline(sketch, "E264", {"points": [v(38.37, -38.07) * mm, v(39.26, -37.4) * mm, v(40.2, -36.1) * mm, v(40.2, -35.57) * mm]});
            skFitSpline(sketch, "E265", {"points": [v(40.2, -35.57) * mm, v(40.2, -35.45) * mm, v(39.98, -35.11) * mm, v(39.7, -34.83) * mm]});
            skFitSpline(sketch, "E266", {"points": [v(39.7, -34.83) * mm, v(38.98, -34.12) * mm, v(38.86, -33.18) * mm, v(39.13, -30.68) * mm]});
            skFitSpline(sketch, "E267", {"points": [v(39.13, -30.68) * mm, v(39.26, -29.5) * mm, v(39.36, -26.93) * mm, v(39.36, -24.95) * mm]});
            skFitSpline(sketch, "E268", {"points": [v(39.36, -24.95) * mm, v(39.36, -21.87) * mm, v(39.3, -21.22) * mm, v(38.94, -20.3) * mm]});
            skFitSpline(sketch, "E269", {"points": [v(38.94, -20.3) * mm, v(38.39, -18.9) * mm, v(38.4, -18.51) * mm, v(39.04, -18) * mm]});
            skFitSpline(sketch, "E270", {"points": [v(39.04, -18) * mm, v(39.45, -17.69) * mm, v(39.57, -17.4) * mm, v(39.57, -16.76) * mm]});
            skFitSpline(sketch, "E271", {"points": [v(39.57, -16.76) * mm, v(39.57, -16.2) * mm, v(39.7, -15.8) * mm, v(39.97, -15.56) * mm]});
            skFitSpline(sketch, "E272", {"points": [v(39.97, -15.56) * mm, v(40.59, -15) * mm, v(40.32, -14.37) * mm, v(39.46, -14.37) * mm]});
            skFitSpline(sketch, "E273", {"points": [v(39.46, -14.37) * mm, v(38.38, -14.37) * mm, v(37.67, -13.4) * mm, v(37.67, -11.9) * mm]});
            skFitSpline(sketch, "E274", {"points": [v(37.67, -11.9) * mm, v(37.67, -10.72) * mm, v(37.93, -9.95) * mm, v(38.44, -9.65) * mm]});
            skFitSpline(sketch, "E275", {"points": [v(38.44, -9.65) * mm, v(39.04, -9.3) * mm, v(38.7, -8.02) * mm, v(38, -8.02) * mm]});
            skFitSpline(sketch, "E276", {"points": [v(38, -8.02) * mm, v(37.74, -8.02) * mm, v(37, -7.64) * mm, v(36.34, -7.18) * mm]});
            skFitSpline(sketch, "E277", {"points": [v(36.34, -7.18) * mm, v(35.18, -6.34) * mm, v(34.43, -6.12) * mm, v(34.18, -6.54) * mm]});
            skFitSpline(sketch, "E278", {"points": [v(34.18, -6.54) * mm, v(34.1, -6.66) * mm, v(33.87, -6.75) * mm, v(33.65, -6.75) * mm]});
            skFitSpline(sketch, "E279", {"points": [v(33.65, -6.75) * mm, v(33.07, -6.75) * mm, v(30.08, -5.09) * mm, v(29.83, -4.63) * mm]});
            skFitSpline(sketch, "E280", {"points": [v(29.83, -4.63) * mm, v(29.5, -4) * mm, v(29.6, -2.89) * mm, v(30.04, -2.22) * mm]});
            skFitSpline(sketch, "E281", {"points": [v(30.04, -2.22) * mm, v(30.4, -1.66) * mm, v(30.41, -1.54) * mm, v(30.14, -1.01) * mm]});
            skFitSpline(sketch, "E282", {"points": [v(30.14, -1.01) * mm, v(29.71, -0.19) * mm, v(29.76, 0.38) * mm, v(30.37, 1.68) * mm]});
            skFitSpline(sketch, "E283", {"points": [v(30.37, 1.68) * mm, v(30.96, 2.95) * mm, v(31, 3.5) * mm, v(30.65, 4.7) * mm]});
            skFitSpline(sketch, "E284", {"points": [v(30.65, 4.7) * mm, v(30.44, 5.4) * mm, v(30.46, 5.58) * mm, v(30.78, 5.93) * mm]});
            skFitSpline(sketch, "E285", {"points": [v(30.78, 5.93) * mm, v(31.13, 6.33) * mm, v(31.13, 6.4) * mm, v(30.68, 7.79) * mm]});
            skFitSpline(sketch, "E286", {"points": [v(30.68, 7.79) * mm, v(30.01, 9.8) * mm, v(29.64, 10.47) * mm, v(28.1, 12.43) * mm]});
            skFitSpline(sketch, "E287", {"points": [v(28.1, 12.43) * mm, v(27.35, 13.37) * mm, v(26.61, 14.44) * mm, v(26.46, 14.8) * mm]});
            skFitSpline(sketch, "E288", {"points": [v(26.46, 14.8) * mm, v(26, 15.95) * mm, v(26.28, 17.5) * mm, v(27.26, 19.16) * mm]});
            skFitSpline(sketch, "E289", {"points": [v(27.26, 19.16) * mm, v(28.4, 21.1) * mm, v(28.53, 21.7) * mm, v(27.93, 22.5) * mm]});
            skFitSpline(sketch, "E290", {"points": [v(27.93, 22.5) * mm, v(27.4, 23.23) * mm, v(27.46, 23.77) * mm, v(28.28, 25.17) * mm]});
            skFitSpline(sketch, "E291", {"points": [v(28.28, 25.17) * mm, v(28.94, 26.3) * mm, v(29.89, 26.9) * mm, v(31.02, 26.9) * mm]});
            skFitSpline(sketch, "E292", {"points": [v(31.02, 26.9) * mm, v(31.6, 26.9) * mm, v(32.1, 27.06) * mm, v(32.48, 27.36) * mm]});
            skFitSpline(sketch, "E293", {"points": [v(32.48, 27.36) * mm, v(33, 27.78) * mm, v(33.05, 27.91) * mm, v(32.96, 28.95) * mm]});
            skFitSpline(sketch, "E294", {"points": [v(32.96, 28.95) * mm, v(32.91, 29.57) * mm, v(32.82, 30.13) * mm, v(32.76, 30.19) * mm]});
            skFitSpline(sketch, "E295", {"points": [v(32.76, 30.19) * mm, v(32.7, 30.25) * mm, v(32.3, 30.15) * mm, v(31.89, 29.97) * mm]});
            skFitSpline(sketch, "E296", {"points": [v(31.89, 29.97) * mm, v(31.46, 29.8) * mm, v(31.06, 29.65) * mm, v(30.98, 29.65) * mm]});
            skFitSpline(sketch, "E297", {"points": [v(30.98, 29.65) * mm, v(30.9, 29.65) * mm, v(30.9, 30.37) * mm, v(30.97, 31.24) * mm]});
            skFitSpline(sketch, "E298", {"points": [v(30.97, 31.24) * mm, v(31.1, 32.73) * mm, v(31.07, 32.83) * mm, v(30.68, 32.83) * mm]});
            skFitSpline(sketch, "E299", {"points": [v(30.68, 32.83) * mm, v(30.45, 32.83) * mm, v(30.26, 32.97) * mm, v(30.26, 33.15) * mm]});
            skFitSpline(sketch, "E300", {"points": [v(30.26, 33.15) * mm, v(30.26, 33.32) * mm, v(30.16, 33.46) * mm, v(30.05, 33.46) * mm]});
            skFitSpline(sketch, "E301", {"points": [v(30.05, 33.46) * mm, v(29.69, 33.46) * mm, v(29.82, 34.44) * mm, v(30.23, 34.81) * mm]});
            skFitSpline(sketch, "E302", {"points": [v(30.23, 34.81) * mm, v(30.44, 35) * mm, v(31.16, 35.28) * mm, v(31.83, 35.42) * mm]});
            skFitSpline(sketch, "E303", {"points": [v(31.83, 35.42) * mm, v(32.85, 35.63) * mm, v(33.13, 35.62) * mm, v(33.6, 35.36) * mm]});
            skFitSpline(sketch, "E304", {"points": [v(33.6, 35.36) * mm, v(34.37, 34.93) * mm, v(34.48, 34.05) * mm, v(33.82, 33.73) * mm]});
            skFitSpline(sketch, "E305", {"points": [v(33.82, 33.73) * mm, v(33.34, 33.51) * mm, v(33.35, 33.5) * mm, v(34.15, 33.16) * mm]});
            skFitSpline(sketch, "E306", {"points": [v(34.15, 33.16) * mm, v(34.9, 32.83) * mm, v(34.99, 32.83) * mm, v(35.36, 33.17) * mm]});
            skFitSpline(sketch, "E307", {"points": [v(35.36, 33.17) * mm, v(35.58, 33.37) * mm, v(35.76, 33.64) * mm, v(35.76, 33.77) * mm]});
            skFitSpline(sketch, "E308", {"points": [v(35.76, 33.77) * mm, v(35.76, 33.9) * mm, v(36.1, 34.7) * mm, v(36.5, 35.56) * mm]});
            skFitSpline(sketch, "E309", {"points": [v(36.5, 35.56) * mm, v(37.29, 37.18) * mm, v(37.3, 37.75) * mm, v(36.61, 38.12) * mm]});
            skFitSpline(sketch, "E310", {"points": [v(36.61, 38.12) * mm, v(36.14, 38.38) * mm, v(35.55, 38.19) * mm, v(35.55, 37.78) * mm]});
            skFitSpline(sketch, "E311", {"points": [v(35.55, 37.78) * mm, v(35.55, 36.66) * mm, v(30.79, 39.12) * mm, v(30.36, 40.45) * mm]});
            skFitSpline(sketch, "E312", {"points": [v(30.36, 40.45) * mm, v(30.3, 40.68) * mm, v(30.34, 41.05) * mm, v(30.47, 41.29) * mm]});
            skFitSpline(sketch, "E313", {"points": [v(30.47, 41.29) * mm, v(30.77, 41.86) * mm, v(31.55, 41.83) * mm, v(33.01, 41.2) * mm]});
            skFitSpline(sketch, "E314", {"points": [v(33.01, 41.2) * mm, v(34.25, 40.67) * mm, v(34.4, 40.66) * mm, v(34.2, 41.18) * mm]});
            skFitSpline(sketch, "E315", {"points": [v(34.2, 41.18) * mm, v(34.13, 41.4) * mm, v(33.81, 41.5) * mm, v(33.34, 41.5) * mm]});
            skFitSpline(sketch, "E316", {"points": [v(33.34, 41.5) * mm, v(32.48, 41.5) * mm, v(32.37, 41.83) * mm, v(32.97, 42.57) * mm]});
            skFitSpline(sketch, "E317", {"points": [v(32.97, 42.57) * mm, v(33.3, 42.96) * mm, v(33.56, 43.04) * mm, v(34.54, 43.04) * mm]});
            skFitSpline(sketch, "E318", {"points": [v(34.54, 43.04) * mm, v(36.05, 43.02) * mm, v(36.12, 43.25) * mm, v(35.4, 45.67) * mm]});
            skFitSpline(sketch, "E319", {"points": [v(35.4, 45.67) * mm, v(34.98, 47.1) * mm, v(34.9, 47.7) * mm, v(35.01, 48.62) * mm]});
            skFitSpline(sketch, "E320", {"points": [v(35.01, 48.62) * mm, v(35.1, 49.37) * mm, v(35.26, 49.76) * mm, v(35.45, 49.76) * mm]});
            skFitSpline(sketch, "E321", {"points": [v(35.45, 49.76) * mm, v(35.79, 49.76) * mm, v(36.46, 48.04) * mm, v(36.81, 46.27) * mm]});
            skFitSpline(sketch, "E322", {"points": [v(36.81, 46.27) * mm, v(37.15, 44.53) * mm, v(37.45, 43.62) * mm, v(37.68, 43.62) * mm]});
            skFitSpline(sketch, "E323", {"points": [v(37.68, 43.62) * mm, v(37.8, 43.62) * mm, v(37.88, 43.84) * mm, v(37.88, 44.1) * mm]});
            skFitSpline(sketch, "E324", {"points": [v(37.88, 44.1) * mm, v(37.88, 44.74) * mm, v(36.88, 48.83) * mm, v(36.6, 49.36) * mm]});
            skFitSpline(sketch, "E325", {"points": [v(36.6, 49.36) * mm, v(36.47, 49.6) * mm, v(36.29, 50.3) * mm, v(36.19, 50.92) * mm]});
            skFitSpline(sketch, "E326", {"points": [v(36.19, 50.92) * mm, v(36.09, 51.54) * mm, v(35.8, 52.48) * mm, v(35.57, 53.01) * mm]});
            skFitSpline(sketch, "E327", {"points": [v(35.57, 53.01) * mm, v(35.31, 53.57) * mm, v(35.13, 54.41) * mm, v(35.13, 55.03) * mm]});
            skFitSpline(sketch, "E328", {"points": [v(35.13, 55.03) * mm, v(35.13, 56.37) * mm, v(34.52, 57.14) * mm, v(33.05, 57.66) * mm]});
            skFitSpline(sketch, "E329", {"points": [v(33.05, 57.66) * mm, v(31.97, 58.05) * mm, v(31.44, 58.5) * mm, v(31.02, 59.34) * mm]});
            skFitSpline(sketch, "E330", {"points": [v(31.02, 59.34) * mm, v(30.64, 60.08) * mm, v(29.4, 60.31) * mm, v(25.6, 60.34) * mm]});
            skFitSpline(sketch, "E331", {"points": [v(25.6, 60.34) * mm, v(21.36, 60.37) * mm, v(20.2, 60.66) * mm, v(19.62, 61.83) * mm]});
            skFitSpline(sketch, "E332", {"points": [v(19.62, 61.83) * mm, v(19.42, 62.24) * mm, v(19.25, 63.05) * mm, v(19.25, 63.63) * mm]});
            skFitSpline(sketch, "E333", {"points": [v(19.25, 63.63) * mm, v(19.24, 64.97) * mm, v(18.71, 66.14) * mm, v(17.39, 67.73) * mm]});
            skFitSpline(sketch, "E334", {"points": [v(17.39, 67.73) * mm, v(15.95, 69.45) * mm, v(15.56, 70.55) * mm, v(15.72, 72.4) * mm]});
            skFitSpline(sketch, "E335", {"points": [v(15.72, 72.4) * mm, v(15.89, 74.42) * mm, v(15.61, 75.26) * mm, v(14.57, 75.97) * mm]});
            skFitSpline(sketch, "E336", {"points": [v(14.57, 75.97) * mm, v(13.8, 76.48) * mm, v(12.94, 77.13) * mm, v(10.52, 78.96) * mm]});
            skFitSpline(sketch, "E337", {"points": [v(10.52, 78.96) * mm, v(9.93, 79.4) * mm, v(9.37, 79.6) * mm, v(8.4, 79.72) * mm]});
            skFitSpline(sketch, "E338", {"points": [v(8.4, 79.72) * mm, v(7.67, 79.8) * mm, v(6.83, 80.05) * mm, v(6.52, 80.27) * mm]});
            skFitSpline(sketch, "E339", {"points": [v(6.52, 80.27) * mm, v(5.73, 80.83) * mm, v(4.99, 80.76) * mm, v(4.18, 80.06) * mm]});
            skFitSpline(sketch, "E340", {"points": [v(4.18, 80.06) * mm, v(3.06, 79.09) * mm, v(2.62, 78.93) * mm, v(1.4, 79.08) * mm]});
            skFitSpline(sketch, "E341", {"points": [v(-1.23, 77.67) * mm, v(-2.35, 76.53) * mm, v(-2.88, 75.8) * mm, v(-3.2, 74.95) * mm]});
            skFitSpline(sketch, "E342", {"points": [v(-3.2, 74.95) * mm, v(-3.44, 74.31) * mm, v(-3.84, 73.58) * mm, v(-4.08, 73.32) * mm]});
            skFitSpline(sketch, "E343", {"points": [v(-4.08, 73.32) * mm, v(-4.6, 72.75) * mm, v(-5.86, 72.28) * mm, v(-7.31, 72.1) * mm]});
            skFitSpline(sketch, "E344", {"points": [v(-7.31, 72.1) * mm, v(-8.5, 71.94) * mm, v(-9.16, 71.58) * mm, v(-9.92, 70.68) * mm]});
            skFitSpline(sketch, "E345", {"points": [v(-9.92, 70.68) * mm, v(-10.62, 69.85) * mm, v(-11.46, 69.45) * mm, v(-12.51, 69.45) * mm]});
            skFitSpline(sketch, "E346", {"points": [v(-13.27, 67.07) * mm, v(-13.12, 64.4) * mm, v(-13.35, 63.34) * mm, v(-14.15, 63) * mm]});
            skFitSpline(sketch, "E347", {"points": [v(-14.15, 63) * mm, v(-14.41, 62.88) * mm, v(-14.68, 62.54) * mm, v(-14.74, 62.25) * mm]});
            skFitSpline(sketch, "E348", {"points": [v(-14.74, 62.25) * mm, v(-14.95, 61.27) * mm, v(-15.22, 60.8) * mm, v(-15.67, 60.66) * mm]});
            skFitSpline(sketch, "E349", {"points": [v(-15.67, 60.66) * mm, v(-16.3, 60.47) * mm, v(-17.15, 61.07) * mm, v(-17.15, 61.71) * mm]});
            skFitSpline(sketch, "E350", {"points": [v(-17.15, 61.71) * mm, v(-17.15, 62.4) * mm, v(-17.57, 62.62) * mm, v(-17.95, 62.12) * mm]});
            skFitSpline(sketch, "E351", {"points": [v(-17.95, 62.12) * mm, v(-18.25, 61.72) * mm, v(-18.24, 60.86) * mm, v(-17.87, 57.55) * mm]});
            skFitSpline(sketch, "E352", {"points": [v(-17.87, 57.55) * mm, v(-17.76, 56.53) * mm, v(-17.83, 56.11) * mm, v(-18.31, 54.9) * mm]});
            skFitSpline(sketch, "E353", {"points": [v(-18.43, 53.1) * mm, v(-18.09, 52.84) * mm, v(-18, 52.61) * mm, v(-18.12, 52.26) * mm]});
            skFitSpline(sketch, "E354", {"points": [v(-18.12, 52.26) * mm, v(-18.35, 51.5) * mm, v(-18.6, 51.29) * mm, v(-19.44, 51.14) * mm]});
            skFitSpline(sketch, "E355", {"points": [v(-19.44, 51.14) * mm, v(-20.16, 51.02) * mm, v(-20.25, 50.92) * mm, v(-20.59, 49.92) * mm]});
            skFitSpline(sketch, "E356", {"points": [v(-20.59, 49.92) * mm, v(-21.07, 48.49) * mm, v(-20.79, 47.82) * mm, v(-19.64, 47.63) * mm]});
            skFitSpline(sketch, "E357", {"points": [v(-19.64, 47.63) * mm, v(-18.7, 47.48) * mm, v(-18.1, 46.98) * mm, v(-17.9, 46.22) * mm]});
            skFitSpline(sketch, "E358", {"points": [v(-17.9, 46.22) * mm, v(-17.82, 45.92) * mm, v(-17.92, 44.77) * mm, v(-18.12, 43.68) * mm]});
            skFitSpline(sketch, "E359", {"points": [v(-18.12, 43.68) * mm, v(-18.44, 41.9) * mm, v(-18.54, 41.66) * mm, v(-19.03, 41.44) * mm]});
            skFitSpline(sketch, "E360", {"points": [v(-19.03, 41.44) * mm, v(-19.33, 41.3) * mm, v(-19.75, 41.02) * mm, v(-19.96, 40.82) * mm]});
            skFitSpline(sketch, "E361", {"points": [v(-19.96, 40.82) * mm, v(-20.16, 40.62) * mm, v(-20.6, 40.45) * mm, v(-20.94, 40.45) * mm]});
            skFitSpline(sketch, "E362", {"points": [v(-21.44, 41.8) * mm, v(-21.32, 43.27) * mm, v(-21.6, 44.43) * mm, v(-22.21, 44.98) * mm]});
            skFitSpline(sketch, "E363", {"points": [v(-22.21, 44.98) * mm, v(-22.54, 45.28) * mm, v(-22.7, 45.3) * mm, v(-23.16, 45.08) * mm]});
            skFitSpline(sketch, "E364", {"points": [v(-23.16, 45.08) * mm, v(-23.48, 44.93) * mm, v(-23.72, 44.65) * mm, v(-23.72, 44.41) * mm]});
            skFitSpline(sketch, "E365", {"points": [v(-23.72, 44.41) * mm, v(-23.72, 44.19) * mm, v(-24.06, 43.69) * mm, v(-24.47, 43.3) * mm]});
            skFitSpline(sketch, "E366", {"points": [v(-24.8, 41.05) * mm, v(-24.28, 39.2) * mm, v(-24.4, 38.43) * mm, v(-25.38, 37) * mm]});
            skFitSpline(sketch, "E367", {"points": [v(-25.38, 37) * mm, v(-26.38, 35.55) * mm, v(-26.52, 35.03) * mm, v(-26.15, 34.3) * mm]});
            skFitSpline(sketch, "E368", {"points": [v(-26.15, 34.3) * mm, v(-25.74, 33.52) * mm, v(-25.75, 32.64) * mm, v(-26.17, 31.34) * mm]});
            skFitSpline(sketch, "E369", {"points": [v(-26.17, 31.34) * mm, v(-26.5, 30.34) * mm, v(-26.5, 30.27) * mm, v(-26.05, 29.35) * mm]});
            skFitSpline(sketch, "E370", {"points": [v(-26.05, 29.35) * mm, v(-25.45, 28.12) * mm, v(-24.64, 27.64) * mm, v(-22.5, 27.27) * mm]});
            skFitSpline(sketch, "E371", {"points": [v(-22.5, 27.27) * mm, v(-21.03, 27.01) * mm, v(-20.71, 27.01) * mm, v(-20.51, 27.25) * mm]});
            skFitSpline(sketch, "E372", {"points": [v(-20.51, 27.25) * mm, v(-20.2, 27.62) * mm, v(-19.6, 27.62) * mm, v(-19.29, 27.24) * mm]});
            skFitSpline(sketch, "E373", {"points": [v(-19.29, 27.24) * mm, v(-18.74, 26.58) * mm, v(-18.77, 25.45) * mm, v(-19.37, 23.93) * mm]});
            skFitSpline(sketch, "E374", {"points": [v(-19.37, 23.93) * mm, v(-19.7, 23.08) * mm, v(-20.07, 22.46) * mm, v(-20.24, 22.46) * mm]});
            skFitSpline(sketch, "E375", {"points": [v(-20.24, 22.46) * mm, v(-20.4, 22.46) * mm, v(-20.54, 22.54) * mm, v(-20.54, 22.65) * mm]});
            skFitSpline(sketch, "E376", {"points": [v(-20.54, 22.65) * mm, v(-20.54, 23.08) * mm, v(-22.27, 25) * mm, v(-22.65, 25) * mm]});
            skFitSpline(sketch, "E377", {"points": [v(-22.65, 25) * mm, v(-23.23, 25) * mm, v(-23.72, 24.2) * mm, v(-23.72, 23.22) * mm]});
            skFitSpline(sketch, "E378", {"points": [v(-23.72, 23.22) * mm, v(-23.72, 22.72) * mm, v(-23.92, 22.04) * mm, v(-24.24, 21.5) * mm]});
            skFitSpline(sketch, "E379", {"points": [v(-24.24, 21.5) * mm, v(-24.66, 20.79) * mm, v(-24.75, 20.34) * mm, v(-24.74, 19.26) * mm]});
            skFitSpline(sketch, "E380", {"points": [v(-24.74, 19.26) * mm, v(-24.72, 18.51) * mm, v(-24.78, 17.69) * mm, v(-24.86, 17.43) * mm]});
            skFitSpline(sketch, "E381", {"points": [v(-24.86, 17.43) * mm, v(-25.08, 16.75) * mm, v(-24.82, 16.1) * mm, v(-24.33, 16.1) * mm]});
            skFitSpline(sketch, "E382", {"points": [v(-24.33, 16.1) * mm, v(-23.36, 16.1) * mm, v(-23.83, 14.55) * mm, v(-24.88, 14.3) * mm]});
            skFitSpline(sketch, "E383", {"points": [v(-24.88, 14.3) * mm, v(-25.3, 14.18) * mm, v(-25.36, 14.09) * mm, v(-25.2, 13.77) * mm]});
            skFitSpline(sketch, "E384", {"points": [v(-25.2, 13.77) * mm, v(-24.96, 13.34) * mm, v(-24.91, 12.23) * mm, v(-25.11, 12.03) * mm]});
            skFitSpline(sketch, "E385", {"points": [v(-25.11, 12.03) * mm, v(-25.18, 11.96) * mm, v(-25.46, 11.98) * mm, v(-25.73, 12.09) * mm]});
            skFitSpline(sketch, "E386", {"points": [v(-25.73, 12.09) * mm, v(-26.03, 12.2) * mm, v(-26.5, 12.18) * mm, v(-26.98, 12.04) * mm]});
            skFitSpline(sketch, "E387", {"points": [v(-26.98, 12.04) * mm, v(-28.78, 11.48) * mm, v(-28.79, 13.48) * mm, v(-26.99, 14.98) * mm]});
            skFitSpline(sketch, "E388", {"points": [v(-26.99, 14.98) * mm, v(-26.47, 15.42) * mm, v(-26.04, 15.92) * mm, v(-26.04, 16.09) * mm]});
            skFitSpline(sketch, "E389", {"points": [v(-26.04, 16.09) * mm, v(-26.04, 16.33) * mm, v(-26.1, 16.35) * mm, v(-26.3, 16.15) * mm]});
            skFitSpline(sketch, "E390", {"points": [v(-26.3, 16.15) * mm, v(-26.76, 15.69) * mm, v(-27.73, 15.86) * mm, v(-28.39, 16.52) * mm]});
            skFitSpline(sketch, "E391", {"points": [v(-28.39, 16.52) * mm, v(-28.98, 17.1) * mm, v(-29, 17.22) * mm, v(-29, 18.97) * mm]});
            skFitSpline(sketch, "E392", {"points": [v(-29, 18.97) * mm, v(-29, 20.63) * mm, v(-29.05, 20.82) * mm, v(-29.43, 20.91) * mm]});
            skFitSpline(sketch, "E393", {"points": [v(-29.43, 20.91) * mm, v(-30.19, 21.11) * mm, v(-29.94, 22.23) * mm, v(-28.69, 24.26) * mm]});
            skFitSpline(sketch, "E394", {"points": [v(-28.69, 24.26) * mm, v(-27.87, 25.58) * mm, v(-28, 27.33) * mm, v(-28.9, 27.33) * mm]});
            skFitSpline(sketch, "E395", {"points": [v(-28.9, 27.33) * mm, v(-29.17, 27.33) * mm, v(-29.7, 27.61) * mm, v(-30.07, 27.96) * mm]});
            skFitSpline(sketch, "E396", {"points": [v(-30.07, 27.96) * mm, v(-30.87, 28.71) * mm, v(-31.12, 28.76) * mm, v(-31.12, 28.14) * mm]});
            skFitSpline(sketch, "E397", {"points": [v(-31.12, 28.14) * mm, v(-31.12, 27.9) * mm, v(-30.7, 27.23) * mm, v(-30.17, 26.67) * mm]});
            skFitSpline(sketch, "E398", {"points": [v(-30.17, 26.67) * mm, v(-29.12, 25.55) * mm, v(-29.07, 25.4) * mm, v(-29.55, 24.9) * mm]});
            skFitSpline(sketch, "E399", {"points": [v(-29.55, 24.9) * mm, v(-30.1, 24.36) * mm, v(-30.96, 24.5) * mm, v(-31.6, 25.23) * mm]});
            skFitSpline(sketch, "E400", {"points": [v(-31.6, 25.23) * mm, v(-32.15, 25.85) * mm, v(-32.25, 25.88) * mm, v(-33.19, 25.74) * mm]});
            skFitSpline(sketch, "E401", {"points": [v(-33.19, 25.74) * mm, v(-34.37, 25.57) * mm, v(-35.26, 25.15) * mm, v(-35.43, 24.68) * mm]});
            skFitSpline(sketch, "E402", {"points": [v(-35.43, 24.68) * mm, v(-35.6, 24.23) * mm, v(-35.14, 24.08) * mm, v(-34.43, 24.35) * mm]});
            skFitSpline(sketch, "E403", {"points": [v(-34.43, 24.35) * mm, v(-34.1, 24.48) * mm, v(-33.54, 24.57) * mm, v(-33.15, 24.57) * mm]});
            skFitSpline(sketch, "E404", {"points": [v(-33.15, 24.57) * mm, v(-32.54, 24.57) * mm, v(-32.46, 24.5) * mm, v(-32.44, 24) * mm]});
            skFitSpline(sketch, "E405", {"points": [v(-32.44, 24) * mm, v(-32.43, 23.67) * mm, v(-32.27, 23.06) * mm, v(-32.1, 22.62) * mm]});
            skFitSpline(sketch, "E406", {"points": [v(-32.1, 22.62) * mm, v(-31.58, 21.42) * mm, v(-31.67, 20.28) * mm, v(-32.4, 18.86) * mm]});
            skFitSpline(sketch, "E407", {"points": [v(-32.4, 18.86) * mm, v(-33.14, 17.4) * mm, v(-33.17, 17.05) * mm, v(-32.63, 16.75) * mm]});
            skFitSpline(sketch, "E408", {"points": [v(-32.63, 16.75) * mm, v(-32.1, 16.47) * mm, v(-31.55, 14.82) * mm, v(-31.55, 13.54) * mm]});
            skFitSpline(sketch, "E409", {"points": [v(-31.55, 13.54) * mm, v(-31.55, 12.77) * mm, v(-31.45, 12.46) * mm, v(-31.11, 12.23) * mm]});
            skFitSpline(sketch, "E410", {"points": [v(-31.11, 12.23) * mm, v(-30.88, 12.06) * mm, v(-30.63, 11.6) * mm, v(-30.56, 11.18) * mm]});
            skFitSpline(sketch, "E411", {"points": [v(-30.56, 11.18) * mm, v(-30.46, 10.56) * mm, v(-30.52, 10.4) * mm, v(-30.91, 10.18) * mm]});
            skFitSpline(sketch, "E412", {"points": [v(-30.91, 10.18) * mm, v(-31.53, 9.85) * mm, v(-32.75, 10.1) * mm, v(-33.03, 10.6) * mm]});
            skFitSpline(sketch, "E413", {"points": [v(-33.03, 10.6) * mm, v(-33.14, 10.82) * mm, v(-33.25, 11.41) * mm, v(-33.26, 11.91) * mm]});
            skFitSpline(sketch, "E414", {"points": [v(-33.26, 11.91) * mm, v(-33.27, 12.53) * mm, v(-33.55, 13.4) * mm, v(-34.16, 14.63) * mm]});
            skFitSpline(sketch, "E415", {"points": [v(-34.16, 14.63) * mm, v(-34.97, 16.28) * mm, v(-35.1, 16.43) * mm, v(-35.72, 16.5) * mm]});
            skFitSpline(sketch, "E416", {"points": [v(-35.72, 16.5) * mm, v(-36.31, 16.55) * mm, v(-36.58, 16.38) * mm, v(-37.73, 15.23) * mm]});
            skFitSpline(sketch, "E417", {"points": [v(-37.73, 15.23) * mm, v(-38.93, 14.04) * mm, v(-39.01, 13.9) * mm, v(-38.59, 13.83) * mm]});
            skFitSpline(sketch, "E418", {"points": [v(-38.59, 13.83) * mm, v(-38.17, 13.76) * mm, v(-38.1, 13.62) * mm, v(-38.11, 12.76) * mm]});
            skFitSpline(sketch, "E419", {"points": [v(-38.11, 12.76) * mm, v(-38.12, 12.21) * mm, v(-38.4, 10.97) * mm, v(-38.75, 9.98) * mm]});
            skFitSpline(sketch, "E420", {"points": [v(-38.75, 9.98) * mm, v(-39.51, 7.8) * mm, v(-39.52, 7.37) * mm, v(-38.83, 5.2) * mm]});
            skFitSpline(sketch, "E421", {"points": [v(-38.83, 5.2) * mm, v(-38.38, 3.8) * mm, v(-38.3, 3.15) * mm, v(-38.32, 1.4) * mm]});
            skFitSpline(sketch, "E422", {"points": [v(-38.32, 1.4) * mm, v(-38.34, 0.23) * mm, v(-38.26, -1.1) * mm, v(-38.13, -1.57) * mm]});
            skFitSpline(sketch, "E423", {"points": [v(-38.13, -1.57) * mm, v(-37.77, -2.92) * mm, v(-37.86, -6.07) * mm, v(-38.34, -8.88) * mm]});
            skFitSpline(sketch, "E424", {"points": [v(-38.34, -8.88) * mm, v(-38.63, -10.58) * mm, v(-38.76, -12.12) * mm, v(-38.71, -13.3) * mm]});
            skFitSpline(sketch, "E425", {"points": [v(-38.71, -13.3) * mm, v(-38.65, -14.92) * mm, v(-38.56, -15.24) * mm, v(-37.96, -16.18) * mm]});
            skFitSpline(sketch, "E426", {"points": [v(-37.41, -20.41) * mm, v(-37.55, -24.06) * mm, v(-37.43, -24.65) * mm, v(-36.22, -26.18) * mm]});
            skFitSpline(sketch, "E427", {"points": [v(-36.22, -26.18) * mm, v(-34.5, -28.36) * mm, v(-33.66, -30.2) * mm, v(-33.66, -31.8) * mm]});
            skFitSpline(sketch, "E428", {"points": [v(-33.66, -31.8) * mm, v(-33.66, -32.5) * mm, v(-33.82, -32.8) * mm, v(-34.62, -33.66) * mm]});
            skFitSpline(sketch, "E429", {"points": [v(-34.62, -33.66) * mm, v(-35.46, -34.56) * mm, v(-35.57, -34.79) * mm, v(-35.57, -35.64) * mm]});
            skFitSpline(sketch, "E430", {"points": [v(-35.57, -35.64) * mm, v(-35.57, -36.85) * mm, v(-35.16, -37.86) * mm, v(-34.2, -38.96) * mm]});
            skFitSpline(sketch, "E431", {"points": [v(-34.2, -38.96) * mm, v(-33.8, -39.44) * mm, v(-33.28, -40.4) * mm, v(-33.04, -41.1) * mm]});
            skFitSpline(sketch, "E432", {"points": [v(-33.04, -41.1) * mm, v(-32.76, -41.93) * mm, v(-32.24, -42.8) * mm, v(-31.56, -43.59) * mm]});
            skFitSpline(sketch, "E433", {"points": [v(-31.56, -43.59) * mm, v(-29.64, -45.8) * mm, v(-29.61, -45.88) * mm, v(-29.6, -49.55) * mm]});
            skFitSpline(sketch, "E434", {"points": [v(-29.6, -49.55) * mm, v(-29.59, -51.33) * mm, v(-29.65, -53.1) * mm, v(-29.74, -53.47) * mm]});
            skFitSpline(sketch, "E435", {"points": [v(-29.74, -53.47) * mm, v(-29.87, -54.05) * mm, v(-29.78, -54.34) * mm, v(-29.2, -55.24) * mm]});
            skFitSpline(sketch, "E436", {"points": [v(-29.2, -55.24) * mm, v(-28.02, -57.1) * mm, v(-28.34, -58.63) * mm, v(-30.4, -60.92) * mm]});
            skFitSpline(sketch, "E437", {"points": [v(-30.9, -63.02) * mm, v(-30.62, -63.56) * mm, v(-29.54, -65.09) * mm, v(-28.5, -66.4) * mm]});
            skFitSpline(sketch, "E438", {"points": [v(-28.5, -66.4) * mm, v(-27.47, -67.73) * mm, v(-25.87, -70.02) * mm, v(-24.93, -71.5) * mm]});
            skFitSpline(sketch, "E439", {"points": [v(-24.93, -71.5) * mm, v(-21.66, -76.64) * mm, v(-20.53, -77.82) * mm, v(-18.3, -78.38) * mm]});
            skFitSpline(sketch, "E440", {"points": [v(-18.3, -78.38) * mm, v(-17.5, -78.58) * mm, v(-15.88, -79.13) * mm, v(-14.72, -79.6) * mm]});
            skFitSpline(sketch, "E441", {"points": [v(-14.72, -79.6) * mm, v(-13.56, -80.07) * mm, v(-12.22, -80.53) * mm, v(-11.76, -80.63) * mm]});
            skFitSpline(sketch, "E442", {"points": [v(-11.76, -80.63) * mm, v(-10.67, -80.86) * mm, v(-8.14, -80.7) * mm, v(-6.84, -80.3) * mm]});
            skFitSpline(sketch, "E443", {"points": [v(-34.5, 19.17) * mm, v(-34.65, 19.34) * mm, v(-35.11, 19.55) * mm, v(-35.54, 19.62) * mm]});
            skFitSpline(sketch, "E444", {"points": [v(-35.54, 19.62) * mm, v(-35.99, 19.7) * mm, v(-36.79, 20.15) * mm, v(-37.44, 20.68) * mm]});
            skFitSpline(sketch, "E445", {"points": [v(-37.44, 20.68) * mm, v(-38.07, 21.2) * mm, v(-38.96, 21.72) * mm, v(-39.42, 21.86) * mm]});
            skFitSpline(sketch, "E446", {"points": [v(-39.42, 21.86) * mm, v(-39.89, 22) * mm, v(-40.41, 22.34) * mm, v(-40.6, 22.6) * mm]});
            skFitSpline(sketch, "E447", {"points": [v(-40.6, 22.6) * mm, v(-40.88, 23.06) * mm, v(-40.88, 23.2) * mm, v(-40.52, 24.1) * mm]});
            skFitSpline(sketch, "E448", {"points": [v(-40.52, 24.1) * mm, v(-39.98, 25.46) * mm, v(-39.97, 28.27) * mm, v(-40.5, 29.07) * mm]});
            skFitSpline(sketch, "E449", {"points": [v(-40.5, 29.07) * mm, v(-40.94, 29.76) * mm, v(-40.96, 30.33) * mm, v(-40.55, 31.12) * mm]});
            skFitSpline(sketch, "E450", {"points": [v(-40.55, 31.12) * mm, v(-40.35, 31.5) * mm, v(-40.29, 32) * mm, v(-40.37, 32.52) * mm]});
            skFitSpline(sketch, "E451", {"points": [v(-40.37, 32.52) * mm, v(-40.49, 33.2) * mm, v(-40.43, 33.39) * mm, v(-39.97, 33.76) * mm]});
            skFitSpline(sketch, "E452", {"points": [v(-39.97, 33.76) * mm, v(-39.45, 34.2) * mm, v(-38.12, 36.16) * mm, v(-37.84, 36.9) * mm]});
            skFitSpline(sketch, "E453", {"points": [v(-37.84, 36.9) * mm, v(-37.74, 37.17) * mm, v(-37.47, 37.27) * mm, v(-36.87, 37.27) * mm]});
            skFitSpline(sketch, "E454", {"points": [v(-36.87, 37.27) * mm, v(-36.4, 37.27) * mm, v(-35.93, 37.4) * mm, v(-35.78, 37.6) * mm]});
            skFitSpline(sketch, "E455", {"points": [v(-35.78, 37.6) * mm, v(-35.64, 37.77) * mm, v(-35.2, 37.9) * mm, v(-34.82, 37.9) * mm]});
            skFitSpline(sketch, "E456", {"points": [v(-34.82, 37.9) * mm, v(-34.13, 37.9) * mm, v(-34.12, 37.9) * mm, v(-34.23, 37.12) * mm]});
            skFitSpline(sketch, "E457", {"points": [v(-34.23, 37.12) * mm, v(-34.47, 35.46) * mm, v(-34.75, 34.75) * mm, v(-35.37, 34.23) * mm]});
            skFitSpline(sketch, "E458", {"points": [v(-35.37, 34.23) * mm, v(-35.99, 33.7) * mm, v(-36, 33.67) * mm, v(-35.67, 33.16) * mm]});
            skFitSpline(sketch, "E459", {"points": [v(-35.67, 33.16) * mm, v(-34.87, 31.95) * mm, v(-36.1, 31.14) * mm, v(-37.5, 31.95) * mm]});
            skFitSpline(sketch, "E460", {"points": [v(-37.5, 31.95) * mm, v(-37.94, 32.2) * mm, v(-38.35, 32.4) * mm, v(-38.4, 32.4) * mm]});
            skFitSpline(sketch, "E461", {"points": [v(-38.4, 32.4) * mm, v(-38.63, 32.4) * mm, v(-38.23, 31.65) * mm, v(-37.44, 30.52) * mm]});
            skFitSpline(sketch, "E462", {"points": [v(-37.44, 30.52) * mm, v(-36.44, 29.1) * mm, v(-36.35, 28.09) * mm, v(-37.16, 27.33) * mm]});
            skFitSpline(sketch, "E463", {"points": [v(-37.16, 27.33) * mm, v(-37.75, 26.77) * mm, v(-37.88, 25.84) * mm, v(-37.36, 25.84) * mm]});
            skFitSpline(sketch, "E464", {"points": [v(-37.36, 25.84) * mm, v(-37.12, 25.84) * mm, v(-37.08, 25.7) * mm, v(-37.18, 25.26) * mm]});
            skFitSpline(sketch, "E465", {"points": [v(-37.18, 25.26) * mm, v(-37.37, 24.47) * mm, v(-37.66, 23.94) * mm, v(-37.9, 23.94) * mm]});
            skFitSpline(sketch, "E466", {"points": [v(-37.9, 23.94) * mm, v(-38.25, 23.94) * mm, v(-38.13, 23.18) * mm, v(-37.73, 22.82) * mm]});
            skFitSpline(sketch, "E467", {"points": [v(-37.73, 22.82) * mm, v(-37.52, 22.63) * mm, v(-36.88, 22.27) * mm, v(-36.3, 22.02) * mm]});
            skFitSpline(sketch, "E468", {"points": [v(-36.3, 22.02) * mm, v(-33.61, 20.87) * mm, v(-33.45, 20.76) * mm, v(-33.45, 20.13) * mm]});
            skFitSpline(sketch, "E469", {"points": [v(-33.45, 20.13) * mm, v(-33.45, 18.94) * mm, v(-33.94, 18.5) * mm, v(-34.5, 19.17) * mm]});
            skFitSpline(sketch, "E470", {"points": [v(-33.88, 20.11) * mm, v(-33.88, 20.2) * mm, v(-34.7, 20.65) * mm, v(-35.7, 21.1) * mm]});
            skFitSpline(sketch, "E471", {"points": [v(-35.7, 21.1) * mm, v(-38.2, 22.21) * mm, v(-38.53, 22.5) * mm, v(-38.53, 23.53) * mm]});
            skFitSpline(sketch, "E472", {"points": [v(-38.53, 23.53) * mm, v(-38.53, 23.99) * mm, v(-38.45, 24.36) * mm, v(-38.35, 24.36) * mm]});
            skFitSpline(sketch, "E473", {"points": [v(-38.35, 24.36) * mm, v(-38.26, 24.36) * mm, v(-38.08, 24.58) * mm, v(-37.96, 24.84) * mm]});
            skFitSpline(sketch, "E474", {"points": [v(-37.96, 24.84) * mm, v(-37.8, 25.2) * mm, v(-37.81, 25.39) * mm, v(-38.03, 25.6) * mm]});
            skFitSpline(sketch, "E475", {"points": [v(-38.03, 25.6) * mm, v(-38.5, 26.03) * mm, v(-38.36, 26.84) * mm, v(-37.67, 27.63) * mm]});
            skFitSpline(sketch, "E476", {"points": [v(-37.67, 27.63) * mm, v(-36.9, 28.51) * mm, v(-36.94, 28.8) * mm, v(-38.14, 30.48) * mm]});
            skFitSpline(sketch, "E477", {"points": [v(-38.14, 30.48) * mm, v(-38.63, 31.17) * mm, v(-38.96, 31.87) * mm, v(-38.96, 32.23) * mm]});
            skFitSpline(sketch, "E478", {"points": [v(-38.96, 32.23) * mm, v(-38.96, 32.75) * mm, v(-38.87, 32.83) * mm, v(-38.36, 32.83) * mm]});
            skFitSpline(sketch, "E479", {"points": [v(-38.36, 32.83) * mm, v(-38.03, 32.83) * mm, v(-37.58, 32.69) * mm, v(-37.36, 32.52) * mm]});
            skFitSpline(sketch, "E480", {"points": [v(-37.36, 32.52) * mm, v(-36.98, 32.23) * mm, v(-36, 32.07) * mm, v(-36, 32.3) * mm]});
            skFitSpline(sketch, "E481", {"points": [v(-36, 32.3) * mm, v(-36, 32.35) * mm, v(-36.15, 32.73) * mm, v(-36.35, 33.14) * mm]});
            skFitSpline(sketch, "E482", {"points": [v(-35.92, 34.57) * mm, v(-35.27, 35.14) * mm, v(-35.1, 35.46) * mm, v(-34.96, 36.38) * mm]});
            skFitSpline(sketch, "E483", {"points": [v(-34.96, 36.38) * mm, v(-34.86, 36.99) * mm, v(-34.82, 37.49) * mm, v(-34.87, 37.49) * mm]});
            skFitSpline(sketch, "E484", {"points": [v(-34.87, 37.49) * mm, v(-34.91, 37.49) * mm, v(-35.23, 37.28) * mm, v(-35.56, 37.04) * mm]});
            skFitSpline(sketch, "E485", {"points": [v(-35.56, 37.04) * mm, v(-35.96, 36.74) * mm, v(-36.36, 36.62) * mm, v(-36.72, 36.69) * mm]});
            skFitSpline(sketch, "E486", {"points": [v(-36.72, 36.69) * mm, v(-37.02, 36.75) * mm, v(-37.26, 36.72) * mm, v(-37.26, 36.64) * mm]});
            skFitSpline(sketch, "E487", {"points": [v(-37.26, 36.64) * mm, v(-37.26, 36.35) * mm, v(-39.4, 33.25) * mm, v(-39.6, 33.25) * mm]});
            skFitSpline(sketch, "E488", {"points": [v(-39.6, 33.25) * mm, v(-39.71, 33.25) * mm, v(-39.8, 32.75) * mm, v(-39.8, 32.14) * mm]});
            skFitSpline(sketch, "E489", {"points": [v(-39.8, 32.14) * mm, v(-39.81, 31.5) * mm, v(-39.95, 30.86) * mm, v(-40.13, 30.62) * mm]});
            skFitSpline(sketch, "E490", {"points": [v(-40.13, 30.62) * mm, v(-40.4, 30.26) * mm, v(-40.4, 30.15) * mm, v(-40.08, 29.67) * mm]});
            skFitSpline(sketch, "E491", {"points": [v(-40.08, 29.67) * mm, v(-39.54, 28.86) * mm, v(-39.43, 25.58) * mm, v(-39.9, 24.18) * mm]});
            skFitSpline(sketch, "E492", {"points": [v(-39.9, 24.18) * mm, v(-40.1, 23.59) * mm, v(-40.2, 23.02) * mm, v(-40.14, 22.92) * mm]});
            skFitSpline(sketch, "E493", {"points": [v(-40.14, 22.92) * mm, v(-40.08, 22.82) * mm, v(-39.57, 22.56) * mm, v(-39.02, 22.35) * mm]});
            skFitSpline(sketch, "E494", {"points": [v(-39.02, 22.35) * mm, v(-38.46, 22.15) * mm, v(-37.5, 21.56) * mm, v(-36.87, 21.05) * mm]});
            skFitSpline(sketch, "E495", {"points": [v(-36.87, 21.05) * mm, v(-36.12, 20.45) * mm, v(-35.53, 20.13) * mm, v(-35.13, 20.13) * mm]});
            skFitSpline(sketch, "E496", {"points": [v(-35.13, 20.13) * mm, v(-34.8, 20.13) * mm, v(-34.48, 20.03) * mm, v(-34.4, 19.91) * mm]});
            skFitSpline(sketch, "E497", {"points": [v(-34.4, 19.91) * mm, v(-34.26, 19.68) * mm, v(-33.88, 19.83) * mm, v(-33.88, 20.11) * mm]});
            skFitSpline(sketch, "E498", {"points": [v(-35.84, 27.25) * mm, v(-35.9, 27.35) * mm, v(-36.01, 27.96) * mm, v(-36.1, 28.6) * mm]});
            skFitSpline(sketch, "E499", {"points": [v(-36.1, 28.6) * mm, v(-36.27, 30.1) * mm, v(-35.9, 30.72) * mm, v(-35.07, 30.34) * mm]});
            skFitSpline(sketch, "E500", {"points": [v(-35.07, 30.34) * mm, v(-34.7, 30.18) * mm, v(-34.56, 29.98) * mm, v(-34.64, 29.77) * mm]});
            skFitSpline(sketch, "E501", {"points": [v(-34.64, 29.77) * mm, v(-34.74, 29.52) * mm, v(-34.61, 29.44) * mm, v(-34.1, 29.44) * mm]});
            skFitSpline(sketch, "E502", {"points": [v(-34.1, 29.44) * mm, v(-33.14, 29.44) * mm, v(-32.6, 29.1) * mm, v(-32.6, 28.48) * mm]});
            skFitSpline(sketch, "E503", {"points": [v(-32.6, 28.48) * mm, v(-32.6, 28.2) * mm, v(-32.71, 27.96) * mm, v(-32.85, 27.96) * mm]});
            skFitSpline(sketch, "E504", {"points": [v(-32.85, 27.96) * mm, v(-32.98, 27.96) * mm, v(-33.2, 27.8) * mm, v(-33.34, 27.62) * mm]});
            skFitSpline(sketch, "E505", {"points": [v(-33.34, 27.62) * mm, v(-33.62, 27.24) * mm, v(-35.65, 26.94) * mm, v(-35.84, 27.25) * mm]});
            skFitSpline(sketch, "E506", {"points": [v(-33.88, 28.07) * mm, v(-33.88, 28.24) * mm, v(-33.73, 28.38) * mm, v(-33.56, 28.38) * mm]});
            skFitSpline(sketch, "E507", {"points": [v(-33.56, 28.38) * mm, v(-33.38, 28.38) * mm, v(-33.24, 28.48) * mm, v(-33.24, 28.6) * mm]});
            skFitSpline(sketch, "E508", {"points": [v(-33.24, 28.6) * mm, v(-33.24, 28.71) * mm, v(-33.73, 28.8) * mm, v(-34.32, 28.8) * mm]});
            skFitSpline(sketch, "E509", {"points": [v(-34.32, 28.8) * mm, v(-35.4, 28.8) * mm, v(-35.4, 28.81) * mm, v(-35.31, 29.43) * mm]});
            skFitSpline(sketch, "E510", {"points": [v(-35.31, 29.43) * mm, v(-35.26, 29.77) * mm, v(-35.3, 30) * mm, v(-35.4, 29.95) * mm]});
            skFitSpline(sketch, "E511", {"points": [v(-35.4, 29.95) * mm, v(-35.6, 29.82) * mm, v(-35.62, 28.91) * mm, v(-35.44, 28.23) * mm]});
            skFitSpline(sketch, "E512", {"points": [v(-35.44, 28.23) * mm, v(-35.33, 27.85) * mm, v(-35.16, 27.75) * mm, v(-34.6, 27.75) * mm]});
            skFitSpline(sketch, "E513", {"points": [v(-34.6, 27.75) * mm, v(-34.1, 27.75) * mm, v(-33.88, 27.85) * mm, v(-33.88, 28.07) * mm]});
            skFitSpline(sketch, "E514", {"points": [v(-34.5, 30.49) * mm, v(-34.87, 31.18) * mm, v(-34.75, 31.97) * mm, v(-34.2, 32.53) * mm]});
            skFitSpline(sketch, "E515", {"points": [v(-34.2, 32.53) * mm, v(-33.9, 32.82) * mm, v(-33.66, 33.2) * mm, v(-33.66, 33.37) * mm]});
            skFitSpline(sketch, "E516", {"points": [v(-33.66, 33.37) * mm, v(-33.66, 33.54) * mm, v(-33.57, 33.68) * mm, v(-33.45, 33.68) * mm]});
            skFitSpline(sketch, "E517", {"points": [v(-33.45, 33.68) * mm, v(-33.34, 33.68) * mm, v(-33.24, 33.6) * mm, v(-33.24, 33.51) * mm]});
            skFitSpline(sketch, "E518", {"points": [v(-33.24, 33.51) * mm, v(-33.24, 33.42) * mm, v(-32.95, 33.24) * mm, v(-32.6, 33.1) * mm]});
            skFitSpline(sketch, "E519", {"points": [v(-32.6, 33.1) * mm, v(-31.72, 32.77) * mm, v(-31.8, 32.27) * mm, v(-32.94, 31.08) * mm]});
            skFitSpline(sketch, "E520", {"points": [v(-32.94, 31.08) * mm, v(-34, 29.96) * mm, v(-34.19, 29.9) * mm, v(-34.5, 30.49) * mm]});
            skFitSpline(sketch, "E521", {"points": [v(-32.6, 32.45) * mm, v(-32.6, 32.54) * mm, v(-32.75, 32.62) * mm, v(-32.92, 32.62) * mm]});
            skFitSpline(sketch, "E522", {"points": [v(-32.92, 32.62) * mm, v(-33.1, 32.62) * mm, v(-33.24, 32.53) * mm, v(-33.24, 32.43) * mm]});
            skFitSpline(sketch, "E523", {"points": [v(-33.24, 32.43) * mm, v(-33.24, 32.33) * mm, v(-33.43, 32.2) * mm, v(-33.66, 32.13) * mm]});
            skFitSpline(sketch, "E524", {"points": [v(-33.66, 32.13) * mm, v(-33.96, 32.06) * mm, v(-34.09, 31.84) * mm, v(-34.09, 31.43) * mm]});
            skFitSpline(sketch, "E525", {"points": [v(-33.35, 31.56) * mm, v(-32.94, 31.95) * mm, v(-32.6, 32.35) * mm, v(-32.6, 32.45) * mm]});
            skSolve(sketch);
        }
        {
            var Q0;
            Q0=makeQuery(id+"F0.imprint","IMPRINT",FACE,{"disambiguationData":[TD([[makeQuery(id+"F0.imprint","IMPRINT",EDGE,{"derivedFrom":sQuery(id+"F0.wireOp",EDGE,"E12")}),1.0]])]});
            var Q1;
            Q1=makeQuery(id+"F0.imprint","IMPRINT",FACE,{"disambiguationData":[TD([[makeQuery(id+"F0.imprint","IMPRINT",EDGE,{"derivedFrom":sQuery(id+"F0.wireOp",EDGE,"E26")}),1.0]])]});
            var Q2;
            Q2=makeQuery(id+"F0.imprint","IMPRINT",FACE,{"disambiguationData":[TD([[makeQuery(id+"F0.imprint","IMPRINT",EDGE,{"derivedFrom":sQuery(id+"F0.wireOp",EDGE,"E506")}),1.0]])]});
            var Q3;
            Q3=makeQuery(id+"F0.imprint","IMPRINT",FACE,{"disambiguationData":[TD([[makeQuery(id+"F0.imprint","IMPRINT",EDGE,{"derivedFrom":sQuery(id+"F0.wireOp",EDGE,"E28")}),1.0]])]});
            extrude(context, id + "F1", {"entities" : qUnion([Q0, Q1, Q2, Q3]), "depth" : 3 * mm, "offsetDistance" : 25 * mm});
        }
        {
            var Q0;
            Q0=makeQuery(id+"F1.opExtrude","CAP_FACE",FACE,{"disambiguationData":[OSD([sQuery(id+"F0.wireOp",EDGE,"E12"),sQuery(id+"F0.wireOp",EDGE,"E13"),sQuery(id+"F0.wireOp",EDGE,"E14"),sQuery(id+"F0.wireOp",EDGE,"E15"),sQuery(id+"F0.wireOp",EDGE,"E16"),sQuery(id+"F0.wireOp",EDGE,"E17"),sQuery(id+"F0.wireOp",EDGE,"E18"),sQuery(id+"F0.wireOp",EDGE,"E19"),sQuery(id+"F0.wireOp",EDGE,"E20"),sQuery(id+"F0.wireOp",EDGE,"E21"),sQuery(id+"F0.wireOp",EDGE,"E22"),sQuery(id+"F0.wireOp",EDGE,"E23"),sQuery(id+"F0.wireOp",EDGE,"E24"),sQuery(id+"F0.wireOp",EDGE,"E25"),sQuery(id+"F0.wireOp",EDGE,"E233"),sQuery(id+"F0.wireOp",EDGE,"E234"),sQuery(id+"F0.wireOp",EDGE,"E235"),sQuery(id+"F0.wireOp",EDGE,"E236"),sQuery(id+"F0.wireOp",EDGE,"E237"),sQuery(id+"F0.wireOp",EDGE,"E238"),sQuery(id+"F0.wireOp",EDGE,"E239"),sQuery(id+"F0.wireOp",EDGE,"E240"),sQuery(id+"F0.wireOp",EDGE,"E241"),sQuery(id+"F0.wireOp",EDGE,"E242"),sQuery(id+"F0.wireOp",EDGE,"E243"),sQuery(id+"F0.wireOp",EDGE,"E244"),sQuery(id+"F0.wireOp",EDGE,"E245"),sQuery(id+"F0.wireOp",EDGE,"E246"),sQuery(id+"F0.wireOp",EDGE,"E247"),sQuery(id+"F0.wireOp",EDGE,"E248"),sQuery(id+"F0.wireOp",EDGE,"E249"),sQuery(id+"F0.wireOp",EDGE,"E250"),sQuery(id+"F0.wireOp",EDGE,"E251"),sQuery(id+"F0.wireOp",EDGE,"E252"),sQuery(id+"F0.wireOp",EDGE,"E253"),sQuery(id+"F0.wireOp",EDGE,"E254"),sQuery(id+"F0.wireOp",EDGE,"E255"),sQuery(id+"F0.wireOp",EDGE,"E256"),sQuery(id+"F0.wireOp",EDGE,"E257"),sQuery(id+"F0.wireOp",EDGE,"E258"),sQuery(id+"F0.wireOp",EDGE,"E259"),sQuery(id+"F0.wireOp",EDGE,"E260"),sQuery(id+"F0.wireOp",EDGE,"E261"),sQuery(id+"F0.wireOp",EDGE,"E262"),sQuery(id+"F0.wireOp",EDGE,"E263"),sQuery(id+"F0.wireOp",EDGE,"E264"),sQuery(id+"F0.wireOp",EDGE,"E265"),sQuery(id+"F0.wireOp",EDGE,"E266"),sQuery(id+"F0.wireOp",EDGE,"E267"),sQuery(id+"F0.wireOp",EDGE,"E268"),sQuery(id+"F0.wireOp",EDGE,"E269"),sQuery(id+"F0.wireOp",EDGE,"E270"),sQuery(id+"F0.wireOp",EDGE,"E271"),sQuery(id+"F0.wireOp",EDGE,"E272"),sQuery(id+"F0.wireOp",EDGE,"E273"),sQuery(id+"F0.wireOp",EDGE,"E274"),sQuery(id+"F0.wireOp",EDGE,"E275"),sQuery(id+"F0.wireOp",EDGE,"E276"),sQuery(id+"F0.wireOp",EDGE,"E277"),sQuery(id+"F0.wireOp",EDGE,"E278"),sQuery(id+"F0.wireOp",EDGE,"E279"),sQuery(id+"F0.wireOp",EDGE,"E280"),sQuery(id+"F0.wireOp",EDGE,"E281"),sQuery(id+"F0.wireOp",EDGE,"E282"),sQuery(id+"F0.wireOp",EDGE,"E283"),sQuery(id+"F0.wireOp",EDGE,"E284"),sQuery(id+"F0.wireOp",EDGE,"E285"),sQuery(id+"F0.wireOp",EDGE,"E286"),sQuery(id+"F0.wireOp",EDGE,"E287"),sQuery(id+"F0.wireOp",EDGE,"E288"),sQuery(id+"F0.wireOp",EDGE,"E289"),sQuery(id+"F0.wireOp",EDGE,"E290"),sQuery(id+"F0.wireOp",EDGE,"E291"),sQuery(id+"F0.wireOp",EDGE,"E292"),sQuery(id+"F0.wireOp",EDGE,"E293"),sQuery(id+"F0.wireOp",EDGE,"E294"),sQuery(id+"F0.wireOp",EDGE,"E295"),sQuery(id+"F0.wireOp",EDGE,"E296"),sQuery(id+"F0.wireOp",EDGE,"E297"),sQuery(id+"F0.wireOp",EDGE,"E298"),sQuery(id+"F0.wireOp",EDGE,"E299"),sQuery(id+"F0.wireOp",EDGE,"E300"),sQuery(id+"F0.wireOp",EDGE,"E301"),sQuery(id+"F0.wireOp",EDGE,"E302"),sQuery(id+"F0.wireOp",EDGE,"E303"),sQuery(id+"F0.wireOp",EDGE,"E304"),sQuery(id+"F0.wireOp",EDGE,"E305"),sQuery(id+"F0.wireOp",EDGE,"E306"),sQuery(id+"F0.wireOp",EDGE,"E307"),sQuery(id+"F0.wireOp",EDGE,"E308"),sQuery(id+"F0.wireOp",EDGE,"E309"),sQuery(id+"F0.wireOp",EDGE,"E310"),sQuery(id+"F0.wireOp",EDGE,"E311"),sQuery(id+"F0.wireOp",EDGE,"E312"),sQuery(id+"F0.wireOp",EDGE,"E313"),sQuery(id+"F0.wireOp",EDGE,"E314"),sQuery(id+"F0.wireOp",EDGE,"E315"),sQuery(id+"F0.wireOp",EDGE,"E316"),sQuery(id+"F0.wireOp",EDGE,"E317"),sQuery(id+"F0.wireOp",EDGE,"E318"),sQuery(id+"F0.wireOp",EDGE,"E319"),sQuery(id+"F0.wireOp",EDGE,"E320"),sQuery(id+"F0.wireOp",EDGE,"E321"),sQuery(id+"F0.wireOp",EDGE,"E322"),sQuery(id+"F0.wireOp",EDGE,"E323"),sQuery(id+"F0.wireOp",EDGE,"E324"),sQuery(id+"F0.wireOp",EDGE,"E325"),sQuery(id+"F0.wireOp",EDGE,"E326"),sQuery(id+"F0.wireOp",EDGE,"E327"),sQuery(id+"F0.wireOp",EDGE,"E328"),sQuery(id+"F0.wireOp",EDGE,"E329"),sQuery(id+"F0.wireOp",EDGE,"E330"),sQuery(id+"F0.wireOp",EDGE,"E331"),sQuery(id+"F0.wireOp",EDGE,"E332"),sQuery(id+"F0.wireOp",EDGE,"E333"),sQuery(id+"F0.wireOp",EDGE,"E334"),sQuery(id+"F0.wireOp",EDGE,"E335"),sQuery(id+"F0.wireOp",EDGE,"E336"),sQuery(id+"F0.wireOp",EDGE,"E337"),sQuery(id+"F0.wireOp",EDGE,"E338"),sQuery(id+"F0.wireOp",EDGE,"E339"),sQuery(id+"F0.wireOp",EDGE,"E340"),sQuery(id+"F0.wireOp",EDGE,"E341"),sQuery(id+"F0.wireOp",EDGE,"E342"),sQuery(id+"F0.wireOp",EDGE,"E343"),sQuery(id+"F0.wireOp",EDGE,"E344"),sQuery(id+"F0.wireOp",EDGE,"E345"),sQuery(id+"F0.wireOp",EDGE,"E346"),sQuery(id+"F0.wireOp",EDGE,"E347"),sQuery(id+"F0.wireOp",EDGE,"E348"),sQuery(id+"F0.wireOp",EDGE,"E349"),sQuery(id+"F0.wireOp",EDGE,"E350"),sQuery(id+"F0.wireOp",EDGE,"E351"),sQuery(id+"F0.wireOp",EDGE,"E352"),sQuery(id+"F0.wireOp",EDGE,"E353"),sQuery(id+"F0.wireOp",EDGE,"E354"),sQuery(id+"F0.wireOp",EDGE,"E355"),sQuery(id+"F0.wireOp",EDGE,"E356"),sQuery(id+"F0.wireOp",EDGE,"E357"),sQuery(id+"F0.wireOp",EDGE,"E358"),sQuery(id+"F0.wireOp",EDGE,"E359"),sQuery(id+"F0.wireOp",EDGE,"E360"),sQuery(id+"F0.wireOp",EDGE,"E361"),sQuery(id+"F0.wireOp",EDGE,"E362"),sQuery(id+"F0.wireOp",EDGE,"E363"),sQuery(id+"F0.wireOp",EDGE,"E364"),sQuery(id+"F0.wireOp",EDGE,"E365"),sQuery(id+"F0.wireOp",EDGE,"E366"),sQuery(id+"F0.wireOp",EDGE,"E367"),sQuery(id+"F0.wireOp",EDGE,"E368"),sQuery(id+"F0.wireOp",EDGE,"E369"),sQuery(id+"F0.wireOp",EDGE,"E370"),sQuery(id+"F0.wireOp",EDGE,"E371"),sQuery(id+"F0.wireOp",EDGE,"E372"),sQuery(id+"F0.wireOp",EDGE,"E373"),sQuery(id+"F0.wireOp",EDGE,"E374"),sQuery(id+"F0.wireOp",EDGE,"E375"),sQuery(id+"F0.wireOp",EDGE,"E376"),sQuery(id+"F0.wireOp",EDGE,"E377"),sQuery(id+"F0.wireOp",EDGE,"E378"),sQuery(id+"F0.wireOp",EDGE,"E379"),sQuery(id+"F0.wireOp",EDGE,"E380"),sQuery(id+"F0.wireOp",EDGE,"E381"),sQuery(id+"F0.wireOp",EDGE,"E382"),sQuery(id+"F0.wireOp",EDGE,"E383"),sQuery(id+"F0.wireOp",EDGE,"E384"),sQuery(id+"F0.wireOp",EDGE,"E385"),sQuery(id+"F0.wireOp",EDGE,"E386"),sQuery(id+"F0.wireOp",EDGE,"E387"),sQuery(id+"F0.wireOp",EDGE,"E388"),sQuery(id+"F0.wireOp",EDGE,"E389"),sQuery(id+"F0.wireOp",EDGE,"E390"),sQuery(id+"F0.wireOp",EDGE,"E391"),sQuery(id+"F0.wireOp",EDGE,"E392"),sQuery(id+"F0.wireOp",EDGE,"E393"),sQuery(id+"F0.wireOp",EDGE,"E394"),sQuery(id+"F0.wireOp",EDGE,"E395"),sQuery(id+"F0.wireOp",EDGE,"E396"),sQuery(id+"F0.wireOp",EDGE,"E397"),sQuery(id+"F0.wireOp",EDGE,"E398"),sQuery(id+"F0.wireOp",EDGE,"E399"),sQuery(id+"F0.wireOp",EDGE,"E400"),sQuery(id+"F0.wireOp",EDGE,"E401"),sQuery(id+"F0.wireOp",EDGE,"E402"),sQuery(id+"F0.wireOp",EDGE,"E403"),sQuery(id+"F0.wireOp",EDGE,"E404"),sQuery(id+"F0.wireOp",EDGE,"E405"),sQuery(id+"F0.wireOp",EDGE,"E406"),sQuery(id+"F0.wireOp",EDGE,"E407"),sQuery(id+"F0.wireOp",EDGE,"E408"),sQuery(id+"F0.wireOp",EDGE,"E409"),sQuery(id+"F0.wireOp",EDGE,"E410"),sQuery(id+"F0.wireOp",EDGE,"E411"),sQuery(id+"F0.wireOp",EDGE,"E412"),sQuery(id+"F0.wireOp",EDGE,"E413"),sQuery(id+"F0.wireOp",EDGE,"E414"),sQuery(id+"F0.wireOp",EDGE,"E415"),sQuery(id+"F0.wireOp",EDGE,"E416"),sQuery(id+"F0.wireOp",EDGE,"E417"),sQuery(id+"F0.wireOp",EDGE,"E418"),sQuery(id+"F0.wireOp",EDGE,"E419"),sQuery(id+"F0.wireOp",EDGE,"E420"),sQuery(id+"F0.wireOp",EDGE,"E421"),sQuery(id+"F0.wireOp",EDGE,"E422"),sQuery(id+"F0.wireOp",EDGE,"E423"),sQuery(id+"F0.wireOp",EDGE,"E424"),sQuery(id+"F0.wireOp",EDGE,"E425"),sQuery(id+"F0.wireOp",EDGE,"E426"),sQuery(id+"F0.wireOp",EDGE,"E427"),sQuery(id+"F0.wireOp",EDGE,"E428"),sQuery(id+"F0.wireOp",EDGE,"E429"),sQuery(id+"F0.wireOp",EDGE,"E430"),sQuery(id+"F0.wireOp",EDGE,"E431"),sQuery(id+"F0.wireOp",EDGE,"E432"),sQuery(id+"F0.wireOp",EDGE,"E433"),sQuery(id+"F0.wireOp",EDGE,"E434"),sQuery(id+"F0.wireOp",EDGE,"E435"),sQuery(id+"F0.wireOp",EDGE,"E436"),sQuery(id+"F0.wireOp",EDGE,"E437"),sQuery(id+"F0.wireOp",EDGE,"E438"),sQuery(id+"F0.wireOp",EDGE,"E439"),sQuery(id+"F0.wireOp",EDGE,"E440"),sQuery(id+"F0.wireOp",EDGE,"E441"),sQuery(id+"F0.wireOp",EDGE,"E442")])],"isStart":false});
            var sketch = newSketch(context, id + "F2", { "sketchPlane" : qUnion([Q0])});
            skLineSegment(sketch, "E526", {"start": v(-18.12, 52.26) * mm, "end": v(-2.72, 52.26) * mm});
            skLineSegment(sketch, "E527", {"start": v(-2.72, 52.26) * mm, "end": v(-2.72, 57.25) * mm});
            skLineSegment(sketch, "E528", {"start": v(-2.72, 57.25) * mm, "end": v(9.81, 57.25) * mm});
            skLineSegment(sketch, "E529", {"start": v(9.81, 57.25) * mm, "end": v(9.81, 54.32) * mm});
            skLineSegment(sketch, "E530", {"start": v(9.81, 54.32) * mm, "end": v(15.66, 54.32) * mm});
            skLineSegment(sketch, "E531", {"start": v(15.66, 54.32) * mm, "end": v(15.66, 46.72) * mm});
            skLineSegment(sketch, "E532", {"start": v(15.66, 46.72) * mm, "end": v(7.64, 37.18) * mm});
            skLineSegment(sketch, "E533", {"start": v(7.64, 37.18) * mm, "end": v(-2.52, 37.18) * mm});
            skLineSegment(sketch, "E534", {"start": v(-2.52, 37.18) * mm, "end": v(-2.52, 39.55) * mm});
            skLineSegment(sketch, "E535", {"start": v(-2.52, 39.55) * mm, "end": v(-24.5, 39.55) * mm});
            skLineSegment(sketch, "E536", {"start": v(15.66, 51.29) * mm, "end": v(21.38, 51.29) * mm});
            skLineSegment(sketch, "E537", {"start": v(21.38, 51.29) * mm, "end": v(21.38, 60.62) * mm});
            skLineSegment(sketch, "E538", {"start": v(7.64, 37.18) * mm, "end": v(7.64, 29.75) * mm});
            skLineSegment(sketch, "E539", {"start": v(7.64, 29.75) * mm, "end": v(12.1, 22.91) * mm});
            skLineSegment(sketch, "E540", {"start": v(12.1, 22.91) * mm, "end": v(27.69, 22.91) * mm});
            skSolve(sketch);
        }
        {
            var Q0;
            Q0=makeQuery(id+"F2.imprint","IMPRINT",FACE,{"disambiguationData":[TD([[makeQuery(id+"F2.imprint","IMPRINT",EDGE,{"derivedFrom":sQuery(id+"F2.wireOp",EDGE,"E526")}),-1.0]])]});
            var Q1;
            Q1=makeQuery(id+"F2.imprint","IMPRINT",FACE,{"disambiguationData":[TD([[makeQuery(id+"F2.imprint","IMPRINT",EDGE,{"derivedFrom":sQuery(id+"F2.wireOp",EDGE,"E526")}),1.0]])]});
            var Q2;
            Q2=makeQuery(id+"F2.imprint","IMPRINT",FACE,{"disambiguationData":[TD([[makeQuery(id+"F2.imprint","IMPRINT",EDGE,{"derivedFrom":sQuery(id+"F2.wireOp",EDGE,"E533")}),1.0]])]});
            extrude(context, id + "F3", {"entities" : qUnion([Q0, Q1, Q2]), "operationType" : NewBodyOperationType.REMOVE, "oppositeDirection" : true, "depth" : 25 * mm, "offsetDistance" : 25 * mm});
        }
    });
